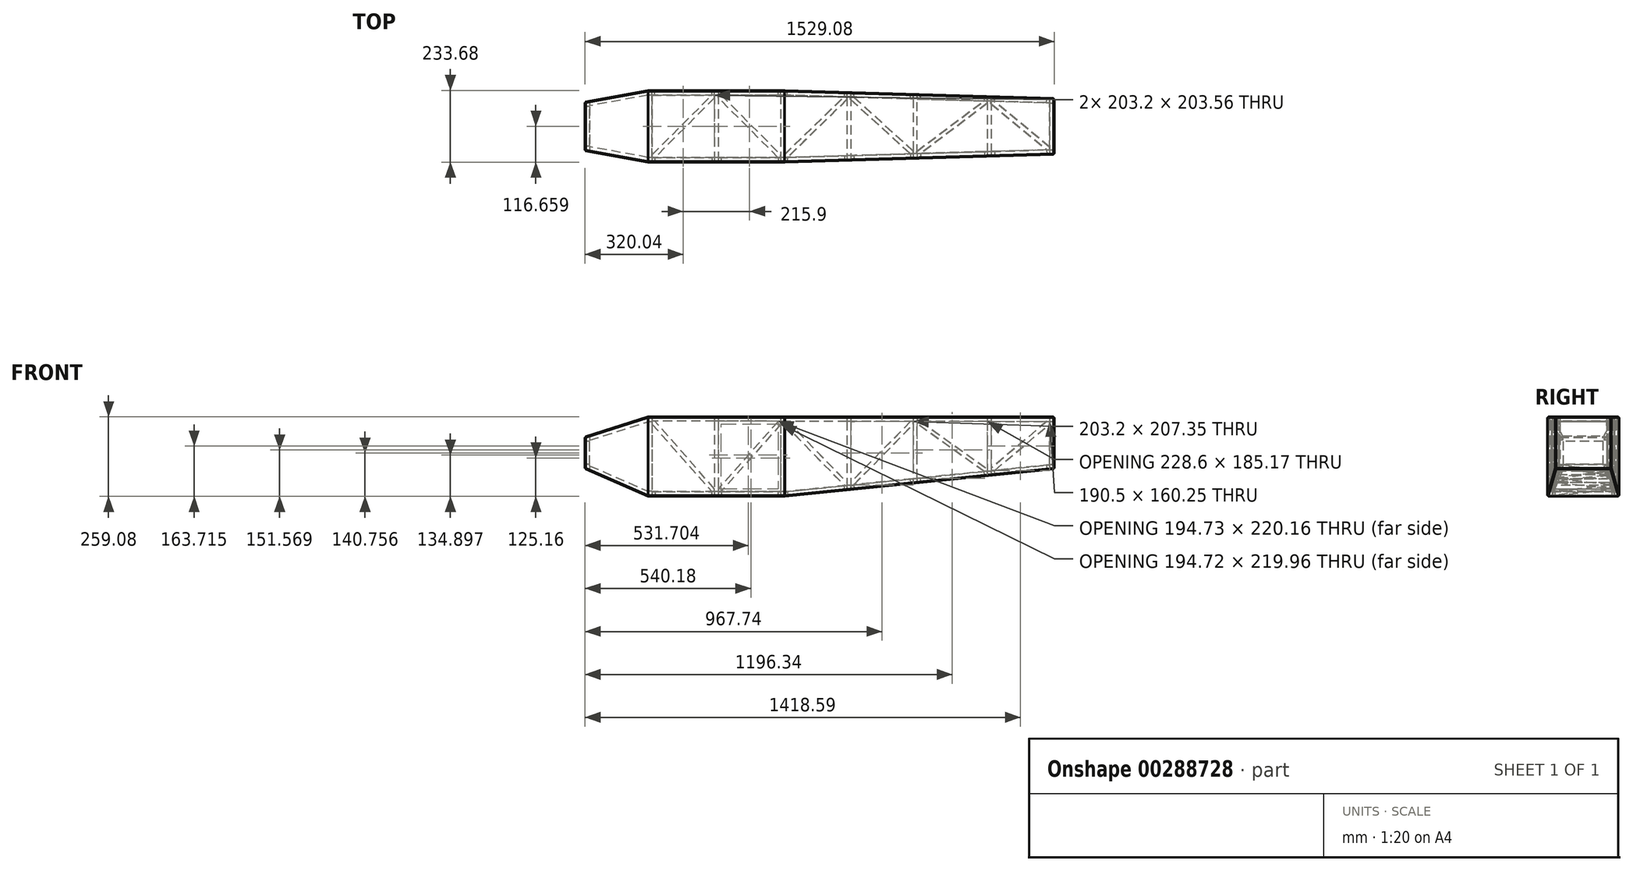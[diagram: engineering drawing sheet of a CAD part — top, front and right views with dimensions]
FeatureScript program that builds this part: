
annotation { "Feature Type Name" : "Feature", "Feature Type Description" : "" }
export const myFeature = defineFeature(function(context is Context, id is Id, definition is map)
    precondition{}
    {
        {
            var Q0;
            Q0=qCreatedBy(makeId("Top.planeOp"),FACE);
            var sketch = newSketch(context, id + "F0", { "sketchPlane" : qUnion([Q0])});
            skLineSegment(sketch, "E0.bottom", {"start": v(762, 177.8) * mm, "end": v(-762, 177.8) * mm});
            skLineSegment(sketch, "E0.top", {"start": v(762, -177.8) * mm, "end": v(-762, -177.8) * mm});
            skLineSegment(sketch, "E0.left", {"start": v(762, 177.8) * mm, "end": v(762, -177.8) * mm});
            skLineSegment(sketch, "E0.right", {"start": v(-762, 177.8) * mm, "end": v(-762, -177.8) * mm});
            skPoint(sketch, "E0.middle", {"position": v(0, 0) * mm});
            skSolve(sketch);
        }
        {
            var Q0;
            Q0=makeQuery(id+"F2.opExtrude","SWEPT_FACE",FACE,{"disambiguationData":[OSD([sQuery(id+"F0.wireOp",EDGE,"E0.top")])]});
            var sketch = newSketch(context, id + "F1", { "sketchPlane" : qUnion([Q0])});
            skLineSegment(sketch, "E1.0", {"start": v(-1003.3, -114.3) * mm, "end": v(1003.3, -114.3) * mm});
            skLineSegment(sketch, "E1.1", {"start": v(-1003.3, 114.3) * mm, "end": v(-1003.3, -114.3) * mm});
            skLineSegment(sketch, "E1.2", {"start": v(1003.3, 114.3) * mm, "end": v(-1003.3, 114.3) * mm});
            skLineSegment(sketch, "E1.3", {"start": v(1003.3, -114.3) * mm, "end": v(1003.3, 114.3) * mm});
            skSolve(sketch);
        }
        {
            var Q0;
            Q0=makeQuery(id+"F0.imprint","IMPRINT",FACE,{"disambiguationData":[TD([[makeQuery(id+"F0.imprint","IMPRINT",EDGE,{"derivedFrom":sQuery(id+"F0.wireOp",EDGE,"E0.bottom")}),1.0]])]});
            extrude(context, id + "F2", {"entities" : qUnion([Q0]), "endBound" : BoundingType.SYMMETRIC, "depth" : 254 * mm});
        }
        {
            var Q0;
            Q0=makeQuery(id+"F2.opExtrude","SWEPT_FACE",FACE,{"disambiguationData":[OSD([sQuery(id+"F0.wireOp",EDGE,"E0.left")])]});
            var sketch = newSketch(context, id + "F3", { "sketchPlane" : qUnion([Q0])});
            skLineSegment(sketch, "E2.0", {"start": v(-165.1, -114.3) * mm, "end": v(165.1, -114.3) * mm});
            skLineSegment(sketch, "E2.1", {"start": v(-165.1, 114.3) * mm, "end": v(-165.1, -114.3) * mm});
            skLineSegment(sketch, "E2.2", {"start": v(165.1, 114.3) * mm, "end": v(-165.1, 114.3) * mm});
            skLineSegment(sketch, "E2.3", {"start": v(165.1, -114.3) * mm, "end": v(165.1, 114.3) * mm});
            skSolve(sketch);
        }
        {
            var Q0;
            Q0=makeQuery(id+"F2.opExtrude","CAP_FACE",FACE,{"disambiguationData":[OSD([sQuery(id+"F0.wireOp",EDGE,"E0.bottom"),sQuery(id+"F0.wireOp",EDGE,"E0.top"),sQuery(id+"F0.wireOp",EDGE,"E0.left"),sQuery(id+"F0.wireOp",EDGE,"E0.right")])],"isStart":false});
            var sketch = newSketch(context, id + "F4", { "sketchPlane" : qUnion([Q0])});
            skLineSegment(sketch, "E3.0", {"start": v(-749.3, -165.1) * mm, "end": v(749.3, -165.1) * mm});
            skLineSegment(sketch, "E3.1", {"start": v(-749.3, 165.1) * mm, "end": v(-749.3, -165.1) * mm});
            skLineSegment(sketch, "E3.2", {"start": v(749.3, 165.1) * mm, "end": v(-749.3, 165.1) * mm});
            skLineSegment(sketch, "E3.3", {"start": v(749.3, -165.1) * mm, "end": v(749.3, 165.1) * mm});
            skSolve(sketch);
        }
        {
            var Q0;
            Q0=qCreatedBy(makeId("Front.planeOp"),FACE);
            var sketch = newSketch(context, id + "F5", { "sketchPlane" : qUnion([Q0])});
            skLineSegment(sketch, "E4.0", {"start": v(-762, 127) * mm, "end": v(-762, -127) * mm, "construction": true});
            skLineSegment(sketch, "E5.bottom", {"start": v(-558.8, -143.07) * mm, "end": v(-546.1, -143.07) * mm});
            skLineSegment(sketch, "E5.top", {"start": v(-558.8, 152.62) * mm, "end": v(-546.1, 152.62) * mm});
            skLineSegment(sketch, "E5.left", {"start": v(-558.8, -143.07) * mm, "end": v(-558.8, 152.62) * mm});
            skLineSegment(sketch, "E5.right", {"start": v(-546.1, -143.07) * mm, "end": v(-546.1, 152.62) * mm});
            skLineSegment(sketch, "E6.bottom", {"start": v(-342.9, -143.07) * mm, "end": v(-330.2, -143.07) * mm});
            skLineSegment(sketch, "E6.top", {"start": v(-342.9, 152.62) * mm, "end": v(-330.2, 152.62) * mm});
            skLineSegment(sketch, "E6.left", {"start": v(-342.9, -143.07) * mm, "end": v(-342.9, 152.62) * mm});
            skLineSegment(sketch, "E6.right", {"start": v(-330.2, -143.07) * mm, "end": v(-330.2, 152.62) * mm});
            skLineSegment(sketch, "E7.bottom", {"start": v(-127, -143.07) * mm, "end": v(-114.3, -143.07) * mm});
            skLineSegment(sketch, "E7.top", {"start": v(-127, 152.62) * mm, "end": v(-114.3, 152.62) * mm});
            skLineSegment(sketch, "E7.left", {"start": v(-127, -143.07) * mm, "end": v(-127, 152.62) * mm});
            skLineSegment(sketch, "E7.right", {"start": v(-114.3, -143.07) * mm, "end": v(-114.3, 152.62) * mm});
            skLineSegment(sketch, "E8.bottom", {"start": v(88.9, -143.07) * mm, "end": v(101.6, -143.07) * mm});
            skLineSegment(sketch, "E8.top", {"start": v(88.9, 152.62) * mm, "end": v(101.6, 152.62) * mm});
            skLineSegment(sketch, "E8.left", {"start": v(88.9, -143.07) * mm, "end": v(88.9, 152.62) * mm});
            skLineSegment(sketch, "E8.right", {"start": v(101.6, -143.07) * mm, "end": v(101.6, 152.62) * mm});
            skLineSegment(sketch, "E9", {"start": v(1356.57, 152.62) * mm, "end": v(-852.45, 152.62) * mm, "construction": true});
            skLineSegment(sketch, "E10", {"start": v(1396.25, -143.07) * mm, "end": v(-846.12, -143.07) * mm, "construction": true});
            skLineSegment(sketch, "E11.bottom", {"start": v(254, 152.62) * mm, "end": v(266.7, 152.62) * mm});
            skLineSegment(sketch, "E11.top", {"start": v(254, -143.07) * mm, "end": v(266.7, -143.07) * mm});
            skLineSegment(sketch, "E12.bottom", {"start": v(546.1, -143.07) * mm, "end": v(558.8, -143.07) * mm});
            skLineSegment(sketch, "E12.top", {"start": v(546.1, 152.62) * mm, "end": v(558.8, 152.62) * mm});
            skLineSegment(sketch, "E12.left", {"start": v(546.1, -143.07) * mm, "end": v(546.1, 152.62) * mm});
            skLineSegment(sketch, "E12.right", {"start": v(558.8, -143.07) * mm, "end": v(558.8, 152.62) * mm});
            skLineSegment(sketch, "E13.bottom", {"start": v(304.8, 152.62) * mm, "end": v(317.5, 152.62) * mm});
            skLineSegment(sketch, "E13.top", {"start": v(304.8, -143.07) * mm, "end": v(317.5, -143.07) * mm});
            skLineSegment(sketch, "E13.left", {"start": v(304.8, 152.62) * mm, "end": v(304.8, -143.07) * mm});
            skLineSegment(sketch, "E13.right", {"start": v(317.5, 152.62) * mm, "end": v(317.5, -143.07) * mm});
            skSolve(sketch);
        }
        {
            var Q0;
            Q0=qSketchRegion(id+"F5",true);
            extrude(context, id + "F6", {"entities" : qUnion([Q0]), "operationType" : NewBodyOperationType.ADD, "endBound" : BoundingType.SYMMETRIC, "depth" : 355.6 * mm});
        }
        {
            var Q0;
            Q0=qCreatedBy(makeId("Front.planeOp"),FACE);
            var sketch = newSketch(context, id + "F7", { "sketchPlane" : qUnion([Q0])});
            skLineSegment(sketch, "E14", {"start": v(-822.55, 43.96) * mm, "end": v(-558.8, 127) * mm});
            skLineSegment(sketch, "E15", {"start": v(-558.8, 127) * mm, "end": v(-1015.01, 307.35) * mm});
            skLineSegment(sketch, "E16", {"start": v(-1015.01, 307.35) * mm, "end": v(-822.55, 43.96) * mm});
            skLineSegment(sketch, "E17.0", {"start": v(-762, 127) * mm, "end": v(-762, -127) * mm, "construction": true});
            skLineSegment(sketch, "E18.0", {"start": v(762, 127) * mm, "end": v(762, -127) * mm, "construction": true});
            skLineSegment(sketch, "E19", {"start": v(-762, -38.1) * mm, "end": v(-558.8, -127) * mm});
            skLineSegment(sketch, "E20", {"start": v(-114.3, -127) * mm, "end": v(762, -38.1) * mm});
            skLineSegment(sketch, "E21", {"start": v(-762, -38.1) * mm, "end": v(-810.44, -38.1) * mm});
            skLineSegment(sketch, "E22", {"start": v(-810.44, -38.1) * mm, "end": v(-810.44, -218.05) * mm});
            skLineSegment(sketch, "E23", {"start": v(-810.44, -218.05) * mm, "end": v(819.71, -218.05) * mm});
            skLineSegment(sketch, "E24", {"start": v(819.71, -218.05) * mm, "end": v(819.71, -38.1) * mm});
            skLineSegment(sketch, "E25", {"start": v(819.71, -38.1) * mm, "end": v(762, -38.1) * mm});
            skLineSegment(sketch, "E26", {"start": v(-114.3, -127) * mm, "end": v(-558.8, -127) * mm});
            skSolve(sketch);
        }
        {
            var Q0;
            Q0=makeQuery(id+"F7.imprint","IMPRINT",FACE,{"disambiguationData":[TD([[makeQuery(id+"F7.imprint","IMPRINT",EDGE,{"derivedFrom":sQuery(id+"F7.wireOp",EDGE,"aae6dbfc-d4bc-4c02-a432-3037b792f5ca")}),1.0]])]});
            var Q1;
            Q1=makeQuery(id+"F7.imprint","IMPRINT",FACE,{"disambiguationData":[TD([[makeQuery(id+"F7.imprint","IMPRINT",EDGE,{"derivedFrom":sQuery(id+"F7.wireOp",EDGE,"E14")}),1.0]])]});
            var Q2;
            Q2=makeQuery(id+"F7.imprint","IMPRINT",FACE,{"disambiguationData":[TD([[makeQuery(id+"F7.imprint","IMPRINT",EDGE,{"derivedFrom":sQuery(id+"F7.wireOp",EDGE,"E19")}),-1.0]])]});
            extrude(context, id + "F8", {"entities" : qUnion([Q0, Q1, Q2]), "operationType" : NewBodyOperationType.REMOVE, "endBound" : BoundingType.SYMMETRIC, "oppositeDirection" : true, "depth" : 381 * mm});
        }
        {
            var Q0;
            Q0=qCreatedBy(makeId("Top.planeOp"),FACE);
            var sketch = newSketch(context, id + "F9", { "sketchPlane" : qUnion([Q0])});
            skLineSegment(sketch, "E27", {"start": v(-925.1, 0) * mm, "end": v(877.17, 0) * mm, "construction": true});
            skLineSegment(sketch, "E28", {"start": v(-885.68, 88.9) * mm, "end": v(840.74, 88.9) * mm, "construction": true});
            skLineSegment(sketch, "E29.0", {"start": v(-762, -177.8) * mm, "end": v(-762, 177.8) * mm, "construction": true});
            skLineSegment(sketch, "E30.0", {"start": v(762, 177.8) * mm, "end": v(762, -177.8) * mm, "construction": true});
            skLineSegment(sketch, "E31.0", {"start": v(-342.9, -368.3) * mm, "end": v(-342.9, -88.9) * mm, "construction": true});
            skLineSegment(sketch, "E32.0", {"start": v(101.6, -177.8) * mm, "end": v(101.6, 177.8) * mm, "construction": true});
            skLineSegment(sketch, "E33", {"start": v(762, 0) * mm, "end": v(762, 88.9) * mm});
            skLineSegment(sketch, "E34.0", {"start": v(-114.3, -177.8) * mm, "end": v(-114.3, 177.8) * mm, "construction": true});
            skLineSegment(sketch, "E35", {"start": v(-762, 77.57) * mm, "end": v(-762, 0) * mm});
            skLineSegment(sketch, "E36", {"start": v(-762, 0) * mm, "end": v(-762, 0) * mm});
            skLineSegment(sketch, "E37.MirrorCS", {"start": v(762, 0) * mm, "end": v(762, -88.9) * mm});
            skLineSegment(sketch, "E38.MirrorCS", {"start": v(-762, -77.57) * mm, "end": v(-762, 0) * mm});
            skLineSegment(sketch, "E39.MirrorCS", {"start": v(-885.68, -88.9) * mm, "end": v(840.74, -88.9) * mm, "construction": true});
            skLineSegment(sketch, "E40.MirrorCS", {"start": v(-762, 177.8) * mm, "end": v(-762, -177.8) * mm, "construction": true});
            skLineSegment(sketch, "E41.MirrorCS", {"start": v(762, -177.8) * mm, "end": v(762, 177.8) * mm, "construction": true});
            skLineSegment(sketch, "E42.MirrorCS", {"start": v(-342.9, 368.3) * mm, "end": v(-342.9, 88.9) * mm, "construction": true});
            skLineSegment(sketch, "E43.MirrorCS", {"start": v(-114.3, 177.8) * mm, "end": v(-114.3, -177.8) * mm, "construction": true});
            skLineSegment(sketch, "E44.MirrorCS", {"start": v(101.6, 177.8) * mm, "end": v(101.6, -177.8) * mm, "construction": true});
            skLineSegment(sketch, "E45.bottom", {"start": v(-858.41, 245.19) * mm, "end": v(858.29, 245.19) * mm});
            skLineSegment(sketch, "E45.top", {"start": v(-858.41, -226.45) * mm, "end": v(858.29, -226.45) * mm});
            skLineSegment(sketch, "E45.left", {"start": v(-858.41, 245.19) * mm, "end": v(-858.41, -226.45) * mm});
            skLineSegment(sketch, "E45.right", {"start": v(858.29, 245.19) * mm, "end": v(858.29, -226.45) * mm});
            skLineSegment(sketch, "E46", {"start": v(-342.9, 114.3) * mm, "end": v(-114.3, 114.3) * mm});
            skLineSegment(sketch, "E47.MirrorCS", {"start": v(-342.9, -114.3) * mm, "end": v(-114.3, -114.3) * mm});
            skLineSegment(sketch, "E48", {"start": v(-342.9, 114.3) * mm, "end": v(-558.8, 114.3) * mm});
            skLineSegment(sketch, "E49", {"start": v(-114.3, 114.3) * mm, "end": v(762, 88.9) * mm});
            skLineSegment(sketch, "E50", {"start": v(-342.9, -114.3) * mm, "end": v(-558.8, -114.3) * mm});
            skLineSegment(sketch, "E51", {"start": v(-114.3, -114.3) * mm, "end": v(762, -88.9) * mm});
            skLineSegment(sketch, "E52", {"start": v(-762, 77.57) * mm, "end": v(-558.8, 114.3) * mm});
            skLineSegment(sketch, "E53", {"start": v(-762, -77.57) * mm, "end": v(-558.8, -114.3) * mm});
            skSolve(sketch);
        }
        {
            var Q0;
            Q0=qSketchRegion(id+"F9",true);
            extrude(context, id + "F10", {"entities" : qUnion([Q0]), "operationType" : NewBodyOperationType.REMOVE, "endBound" : BoundingType.SYMMETRIC, "oppositeDirection" : true, "depth" : 381 * mm});
        }
        {
            var Q0;
            Q0=qCreatedBy(makeId("Top.planeOp"),FACE);
            var sketch = newSketch(context, id + "F11", { "sketchPlane" : qUnion([Q0])});
            skLineSegment(sketch, "E54.1", {"start": v(-749.3, -66.96) * mm, "end": v(-749.3, 66.96) * mm});
            skLineSegment(sketch, "E55.1", {"start": v(749.3, 76.56) * mm, "end": v(749.3, -76.56) * mm});
            skLineSegment(sketch, "E56.0", {"start": v(-127, 101.6) * mm, "end": v(-330.2, 101.6) * mm});
            skLineSegment(sketch, "E57.0", {"start": v(-330.2, -101.96) * mm, "end": v(-127, -101.96) * mm});
            skLineSegment(sketch, "E58.0", {"start": v(558.8, 82.08) * mm, "end": v(749.3, 76.56) * mm});
            skLineSegment(sketch, "E59.0", {"start": v(558.8, -82.08) * mm, "end": v(749.3, -76.56) * mm});
            skLineSegment(sketch, "E60.0", {"start": v(-749.3, -66.96) * mm, "end": v(-558.8, -101.4) * mm});
            skLineSegment(sketch, "E61", {"start": v(-342.9, -101.96) * mm, "end": v(-546.1, -101.96) * mm});
            skLineSegment(sketch, "E62", {"start": v(-546.1, 101.6) * mm, "end": v(-342.9, 101.6) * mm});
            skLineSegment(sketch, "E63.0.1", {"start": v(-546.1, -101.96) * mm, "end": v(-546.1, 101.6) * mm});
            skLineSegment(sketch, "E63.0.3", {"start": v(-558.8, 101.4) * mm, "end": v(-558.8, -101.4) * mm});
            skLineSegment(sketch, "E64.0.1", {"start": v(-342.9, 101.6) * mm, "end": v(-342.9, -101.96) * mm});
            skLineSegment(sketch, "E65.0.1", {"start": v(88.9, 95.71) * mm, "end": v(88.9, -95.7) * mm});
            skLineSegment(sketch, "E65.0.3", {"start": v(101.6, -95.34) * mm, "end": v(101.6, 95.34) * mm});
            skLineSegment(sketch, "E66.0.1", {"start": v(304.8, 89.45) * mm, "end": v(304.8, -89.45) * mm});
            skLineSegment(sketch, "E66.0.3", {"start": v(317.5, -89.08) * mm, "end": v(317.5, 89.08) * mm});
            skLineSegment(sketch, "E67.0.1", {"start": v(546.1, 82.45) * mm, "end": v(546.1, -82.45) * mm});
            skLineSegment(sketch, "E67.0.3", {"start": v(558.8, -82.08) * mm, "end": v(558.8, 82.08) * mm});
            skLineSegment(sketch, "E68.trimOffspring", {"start": v(304.8, -89.45) * mm, "end": v(101.6, -95.34) * mm});
            skLineSegment(sketch, "E69.trimOffspring", {"start": v(88.9, -95.7) * mm, "end": v(-114.3, -101.6) * mm});
            skLineSegment(sketch, "E70.trimOffspring", {"start": v(101.6, 95.34) * mm, "end": v(304.8, 89.45) * mm});
            skPoint(sketch, "E63.0.2.end.orphan", {"position": v(-558.8, 114.3) * mm});
            skPoint(sketch, "E63.0.2.start.orphan", {"position": v(-546.1, 114.3) * mm});
            skPoint(sketch, "E71.orphan", {"position": v(-558.8, -114.3) * mm});
            skPoint(sketch, "E72.orphan", {"position": v(-546.1, -114.3) * mm});
            skLineSegment(sketch, "E73", {"start": v(-749.3, 66.96) * mm, "end": v(-558.8, 101.4) * mm});
            skLineSegment(sketch, "E74", {"start": v(-114.3, -101.6) * mm, "end": v(-114.3, 101.6) * mm});
            skLineSegment(sketch, "E75", {"start": v(-330.2, 101.6) * mm, "end": v(-330.2, -101.96) * mm});
            skLineSegment(sketch, "E76", {"start": v(-127, 101.6) * mm, "end": v(-127, -101.96) * mm});
            skLineSegment(sketch, "E77", {"start": v(546.1, -82.45) * mm, "end": v(317.5, -89.08) * mm});
            skLineSegment(sketch, "E78", {"start": v(88.9, 95.71) * mm, "end": v(-114.3, 101.6) * mm});
            skLineSegment(sketch, "E79", {"start": v(546.1, 82.45) * mm, "end": v(317.5, 89.08) * mm});
            skSolve(sketch);
        }
        {
            var Q0;
            Q0=qSketchRegion(id+"F11",true);
            extrude(context, id + "F12", {"entities" : qUnion([Q0]), "operationType" : NewBodyOperationType.REMOVE, "endBound" : BoundingType.SYMMETRIC, "depth" : 381 * mm});
        }
        {
            var Q0;
            Q0=qCreatedBy(makeId("Front.planeOp"),FACE);
            var sketch = newSketch(context, id + "F13", { "sketchPlane" : qUnion([Q0])});
            skLineSegment(sketch, "E80.0", {"start": v(-749.3, 53.7) * mm, "end": v(-558.8, 113.69) * mm});
            skLineSegment(sketch, "E80.1", {"start": v(-749.3, -29.8) * mm, "end": v(-749.3, 53.7) * mm});
            skLineSegment(sketch, "E80.2", {"start": v(-749.3, -29.8) * mm, "end": v(-558.8, -113.14) * mm});
            skLineSegment(sketch, "E80.3", {"start": v(-342.9, -114.3) * mm, "end": v(-546.1, -114.3) * mm});
            skLineSegment(sketch, "E81.0", {"start": v(749.3, -26.62) * mm, "end": v(558.8, -45.95) * mm});
            skLineSegment(sketch, "E81.1", {"start": v(749.3, -26.62) * mm, "end": v(749.3, 114.3) * mm});
            skLineSegment(sketch, "E81.2", {"start": v(558.8, 114.3) * mm, "end": v(749.3, 114.3) * mm});
            skLineSegment(sketch, "E82", {"start": v(-127, -114.36) * mm, "end": v(-330.2, -114.3) * mm});
            skLineSegment(sketch, "E83.0.1", {"start": v(558.8, 114.3) * mm, "end": v(558.8, -45.95) * mm});
            skLineSegment(sketch, "E84.0.1", {"start": v(101.6, 114.89) * mm, "end": v(101.6, -92.46) * mm});
            skLineSegment(sketch, "E84.0.3", {"start": v(304.8, -71.84) * mm, "end": v(304.8, 114.63) * mm});
            skLineSegment(sketch, "E85.0.0", {"start": v(-330.2, 115.44) * mm, "end": v(-330.2, -114.3) * mm});
            skLineSegment(sketch, "E85.0.2", {"start": v(-127, -114.36) * mm, "end": v(-127, 115.18) * mm});
            skLineSegment(sketch, "E86.0.1", {"start": v(-546.1, 115.71) * mm, "end": v(-546.1, -114.3) * mm});
            skLineSegment(sketch, "E86.0.3", {"start": v(-342.9, -114.3) * mm, "end": v(-342.9, 115.45) * mm});
            skLineSegment(sketch, "E87.0.2", {"start": v(-558.8, -113.14) * mm, "end": v(-558.8, 113.69) * mm});
            skPoint(sketch, "E83.0.0.start.orphan", {"position": v(749.3, 127) * mm});
            skPoint(sketch, "E88.orphan", {"position": v(558.8, 127) * mm});
            skPoint(sketch, "E89.0.0.start.orphan", {"position": v(558.8, 126.99) * mm});
            skLineSegment(sketch, "E90.trimOffspring", {"start": v(304.8, 114.63) * mm, "end": v(101.6, 114.89) * mm});
            skPoint(sketch, "E84.0.0.start.orphan", {"position": v(304.8, 127) * mm});
            skLineSegment(sketch, "E91.trimOffspring", {"start": v(-127, 115.18) * mm, "end": v(-330.2, 115.44) * mm});
            skPoint(sketch, "E85.0.1.end.orphan", {"position": v(-127, -127) * mm});
            skPoint(sketch, "E92.orphan", {"position": v(-330.2, -127) * mm});
            skLineSegment(sketch, "E93.trimOffspring", {"start": v(-342.9, 115.45) * mm, "end": v(-546.1, 115.71) * mm});
            skPoint(sketch, "E85.0.3.end.orphan", {"position": v(-330.2, 127) * mm});
            skPoint(sketch, "E85.0.3.start.orphan", {"position": v(-127, 127) * mm});
            skPoint(sketch, "E86.0.2.end.orphan", {"position": v(-342.9, -127) * mm});
            skPoint(sketch, "E94.orphan", {"position": v(-546.1, -127) * mm});
            skPoint(sketch, "E95.orphan", {"position": v(-546.1, 127) * mm});
            skPoint(sketch, "E87.0.3.start.orphan", {"position": v(-558.8, 127) * mm});
            skPoint(sketch, "E96.orphan", {"position": v(101.6, 127) * mm});
            skLineSegment(sketch, "E97", {"start": v(546.1, -48.1) * mm, "end": v(456.3, -56.47) * mm});
            skPoint(sketch, "E83.0.2.end.orphan", {"position": v(749.3, -39.39) * mm});
            skPoint(sketch, "E98.orphan", {"position": v(-342.9, 127) * mm});
            skLineSegment(sketch, "E99.left", {"start": v(-680.76, 244.02) * mm, "end": v(-680.76, 242.67) * mm});
            skLineSegment(sketch, "E99.right", {"start": v(-640.08, 244.02) * mm, "end": v(-640.08, 242.67) * mm});
            skLineSegment(sketch, "E100.bottom", {"start": v(851.63, 270.75) * mm, "end": v(-718.73, 270.75) * mm});
            skLineSegment(sketch, "E100.top", {"start": v(851.63, 127) * mm, "end": v(-718.73, 127) * mm});
            skLineSegment(sketch, "E100.left", {"start": v(851.63, 270.75) * mm, "end": v(851.63, 127) * mm});
            skLineSegment(sketch, "E100.right", {"start": v(-718.73, 270.75) * mm, "end": v(-718.73, 127) * mm});
            skLineSegment(sketch, "E101", {"start": v(-114.3, -114.36) * mm, "end": v(88.9, -93.75) * mm});
            skLineSegment(sketch, "E102", {"start": v(546.1, 114.3) * mm, "end": v(317.5, 114.61) * mm});
            skLineSegment(sketch, "E103", {"start": v(88.9, 114.9) * mm, "end": v(-114.3, 115.18) * mm});
            skLineSegment(sketch, "E104", {"start": v(-114.3, 115.18) * mm, "end": v(-114.3, -114.36) * mm});
            skLineSegment(sketch, "E105", {"start": v(88.9, 114.9) * mm, "end": v(88.9, -93.75) * mm});
            skLineSegment(sketch, "E106", {"start": v(317.5, 114.61) * mm, "end": v(317.5, -70.55) * mm});
            skLineSegment(sketch, "E107", {"start": v(546.1, 114.3) * mm, "end": v(546.1, -48.1) * mm});
            skLineSegment(sketch, "E108.trimOffspring", {"start": v(317.5, -70.55) * mm, "end": v(456.3, -56.47) * mm});
            skLineSegment(sketch, "E109.trimOffspring", {"start": v(101.6, -92.46) * mm, "end": v(304.8, -71.84) * mm});
            skSolve(sketch);
        }
        {
            var Q0;
            Q0=qSketchRegion(id+"F13",true);
            extrude(context, id + "F14", {"entities" : qUnion([Q0]), "operationType" : NewBodyOperationType.REMOVE, "endBound" : BoundingType.SYMMETRIC, "oppositeDirection" : true, "depth" : 381 * mm});
        }
        {
            var Q0;
            {var subQ4=sQuery(id+"F5.wireOp",EDGE,"E5.top");var subQ11=sQuery(id+"F5.wireOp",EDGE,"E5.left");Q0=makeQuery(id+"F14.boolean.opBoolean","MERGE",FACE,{"derivedFrom":[makeQuery(id+"F12.boolean.opBoolean","MERGE",FACE,{"derivedFrom":[makeQuery(id+"F6.boolean.opBoolean","SPLIT",FACE,{"disambiguationData":[TD([makeQuery(id+"F6.opExtrude","SWEPT_FACE",FACE,{"disambiguationData":[OSD([subQ4])]})])],"derivedFrom":makeQuery(id+"F6.opExtrude","SWEPT_FACE",FACE,{"disambiguationData":[OSD([subQ11])]})}),makeQuery(id+"F12.opExtrude","SWEPT_FACE",FACE,{"disambiguationData":[OSD([sQuery(id+"F11.wireOp",EDGE,"76c89935-962c-43c5-8293-adbbc792d1c5.0")])]})]}),makeQuery(id+"F14.opExtrude","SWEPT_FACE",FACE,{"disambiguationData":[OSD([sQuery(id+"F13.wireOp",EDGE,"9ef2c277-a94d-4be6-9fd4-f6ea86bf56da.0.3")])]})]});}
            var sketch = newSketch(context, id + "F15", { "sketchPlane" : qUnion([Q0])});
            skLineSegment(sketch, "E110.bottom", {"start": v(-101.4, 113.69) * mm, "end": v(101.4, 113.69) * mm});
            skLineSegment(sketch, "E110.top", {"start": v(-101.4, -113.14) * mm, "end": v(101.4, -113.14) * mm});
            skLineSegment(sketch, "E110.left", {"start": v(-101.4, 113.69) * mm, "end": v(-101.4, -113.14) * mm});
            skLineSegment(sketch, "E110.right", {"start": v(101.4, 113.69) * mm, "end": v(101.4, -113.14) * mm});
            skSolve(sketch);
        }
        {
            var Q0;
            Q0=qSketchRegion(id+"F15",true);
            extrude(context, id + "F16", {"entities" : qUnion([Q0]), "operationType" : NewBodyOperationType.REMOVE, "oppositeDirection" : true, "depth" : 25.4 * mm});
        }
        {
            var Q0;
            {var subQ1=sQuery(id+"F5.wireOp",EDGE,"E6.left");var subQ2=sQuery(id+"F5.wireOp",EDGE,"E6.top");Q0=makeQuery(id+"F14.boolean.opBoolean","MERGE",FACE,{"derivedFrom":[makeQuery(id+"F12.boolean.opBoolean","MERGE",FACE,{"derivedFrom":[makeQuery(id+"F6.boolean.opBoolean","SPLIT",FACE,{"disambiguationData":[TD([makeQuery(id+"F6.opExtrude","SWEPT_FACE",FACE,{"disambiguationData":[OSD([subQ2])]})])],"derivedFrom":makeQuery(id+"F6.opExtrude","SWEPT_FACE",FACE,{"disambiguationData":[OSD([subQ1])]})}),makeQuery(id+"F12.opExtrude","SWEPT_FACE",FACE,{"disambiguationData":[OSD([sQuery(id+"F11.wireOp",EDGE,"7b3102ac-ed15-4f5d-bc17-57cfcd7eebf1.0")])]})]}),makeQuery(id+"F14.opExtrude","SWEPT_FACE",FACE,{"disambiguationData":[OSD([sQuery(id+"F13.wireOp",EDGE,"8vpACN4d-Oada-hr1t-Xb63-NezVnV2j5PEM")])]})]});}
            var sketch = newSketch(context, id + "F17", { "sketchPlane" : qUnion([Q0])});
            skLineSegment(sketch, "E111.bottom", {"start": v(-101.6, 115.45) * mm, "end": v(101.96, 115.45) * mm});
            skLineSegment(sketch, "E111.top", {"start": v(-101.6, -114.3) * mm, "end": v(101.96, -114.3) * mm});
            skLineSegment(sketch, "E111.left", {"start": v(-101.6, 115.45) * mm, "end": v(-101.6, -114.3) * mm});
            skLineSegment(sketch, "E111.right", {"start": v(101.96, 115.45) * mm, "end": v(101.96, -114.3) * mm});
            skSolve(sketch);
        }
        {
            var Q0;
            Q0=qSketchRegion(id+"F17",true);
            extrude(context, id + "F18", {"entities" : qUnion([Q0]), "operationType" : NewBodyOperationType.REMOVE, "oppositeDirection" : true, "depth" : 25.4 * mm});
        }
        {
            var Q0;
            {var subQ8=sQuery(id+"F5.wireOp",EDGE,"E7.top");var subQ16=sQuery(id+"F5.wireOp",EDGE,"E7.left");Q0=makeQuery(id+"F14.boolean.opBoolean","MERGE",FACE,{"derivedFrom":[makeQuery(id+"F12.boolean.opBoolean","MERGE",FACE,{"derivedFrom":[makeQuery(id+"F6.boolean.opBoolean","SPLIT",FACE,{"disambiguationData":[TD([makeQuery(id+"F6.opExtrude","SWEPT_FACE",FACE,{"disambiguationData":[OSD([subQ8])]})])],"derivedFrom":makeQuery(id+"F6.opExtrude","SWEPT_FACE",FACE,{"disambiguationData":[OSD([subQ16])]})}),makeQuery(id+"F12.opExtrude","SWEPT_FACE",FACE,{"disambiguationData":[OSD([sQuery(id+"F11.wireOp",EDGE,"b35c1112-db7b-4928-a18e-9a17467dcdab.0")])]})]}),makeQuery(id+"F14.opExtrude","SWEPT_FACE",FACE,{"disambiguationData":[OSD([sQuery(id+"F13.wireOp",EDGE,"fa40cc79-636a-4cbc-a25d-f27d8fe22ac2.0.3")])]})]});}
            var sketch = newSketch(context, id + "F19", { "sketchPlane" : qUnion([Q0])});
            skLineSegment(sketch, "E112.bottom", {"start": v(-101.6, 115.18) * mm, "end": v(101.96, 115.18) * mm});
            skLineSegment(sketch, "E112.top", {"start": v(-101.6, -114.36) * mm, "end": v(101.96, -114.36) * mm});
            skLineSegment(sketch, "E112.left", {"start": v(-101.6, 115.18) * mm, "end": v(-101.6, -114.36) * mm});
            skLineSegment(sketch, "E112.right", {"start": v(101.96, 115.18) * mm, "end": v(101.96, -114.36) * mm});
            skSolve(sketch);
        }
        {
            var Q0;
            Q0=qSketchRegion(id+"F19",true);
            extrude(context, id + "F20", {"entities" : qUnion([Q0]), "operationType" : NewBodyOperationType.REMOVE, "oppositeDirection" : true, "depth" : 25.4 * mm});
        }
        {
            var Q0;
            {var subQ0=sQuery(id+"F5.wireOp",EDGE,"E8.bottom");var subQ36=sQuery(id+"F5.wireOp",EDGE,"E8.left");var subQ37=sQuery(id+"F5.wireOp",EDGE,"E8.top");var subQ60=makeQuery(id+"F6.opExtrude","SWEPT_FACE",FACE,{"disambiguationData":[OSD([subQ36])]});Q0=makeQuery(id+"F14.boolean.opBoolean","MERGE",FACE,{"derivedFrom":[makeQuery(id+"F12.boolean.opBoolean","MERGE",FACE,{"derivedFrom":[makeQuery(id+"F6.boolean.opBoolean","SPLIT",FACE,{"disambiguationData":[TD([makeQuery(id+"F6.opExtrude","SWEPT_FACE",FACE,{"disambiguationData":[OSD([subQ37])]})])],"derivedFrom":subQ60}),makeQuery(id+"F6.boolean.opBoolean","SPLIT",FACE,{"disambiguationData":[TD([makeQuery(id+"F6.opExtrude","SWEPT_FACE",FACE,{"disambiguationData":[OSD([subQ0])]})])],"derivedFrom":subQ60}),makeQuery(id+"F12.opExtrude","SWEPT_FACE",FACE,{"disambiguationData":[OSD([sQuery(id+"F11.wireOp",EDGE,"7310f20e-b108-4276-8773-8cf4f74fe12c.0")])]})]}),makeQuery(id+"F14.opExtrude","SWEPT_FACE",FACE,{"disambiguationData":[OSD([sQuery(id+"F13.wireOp",EDGE,"FrRoJ9V7-tiAn-pTb4-UzEj-WxOpO9FH2ecp")])]})]});}
            var sketch = newSketch(context, id + "F21", { "sketchPlane" : qUnion([Q0])});
            skLineSegment(sketch, "E113.bottom", {"start": v(-95.71, 114.9) * mm, "end": v(95.7, 114.9) * mm});
            skLineSegment(sketch, "E113.top", {"start": v(-95.71, -93.75) * mm, "end": v(95.7, -93.75) * mm});
            skLineSegment(sketch, "E113.left", {"start": v(-95.71, 114.9) * mm, "end": v(-95.71, -93.75) * mm});
            skLineSegment(sketch, "E113.right", {"start": v(95.7, 114.9) * mm, "end": v(95.7, -93.75) * mm});
            skSolve(sketch);
        }
        {
            var Q0;
            Q0=qSketchRegion(id+"F21",true);
            extrude(context, id + "F22", {"entities" : qUnion([Q0]), "operationType" : NewBodyOperationType.REMOVE, "oppositeDirection" : true, "depth" : 25.4 * mm});
        }
        {
            var Q0;
            {var subQ35=sQuery(id+"F5.wireOp",EDGE,"E13.left");var subQ37=sQuery(id+"F5.wireOp",EDGE,"E13.bottom");Q0=makeQuery(id+"F14.boolean.opBoolean","MERGE",FACE,{"derivedFrom":[makeQuery(id+"F12.boolean.opBoolean","MERGE",FACE,{"derivedFrom":[makeQuery(id+"F6.boolean.opBoolean","SPLIT",FACE,{"disambiguationData":[TD([makeQuery(id+"F6.opExtrude","SWEPT_FACE",FACE,{"disambiguationData":[OSD([subQ37])]})])],"derivedFrom":makeQuery(id+"F6.opExtrude","SWEPT_FACE",FACE,{"disambiguationData":[OSD([subQ35])]})}),makeQuery(id+"F12.opExtrude","SWEPT_FACE",FACE,{"disambiguationData":[OSD([sQuery(id+"F11.wireOp",EDGE,"b7ba8543-acbf-43cf-88d8-2159336d2e7e.0")])]})]}),makeQuery(id+"F14.opExtrude","SWEPT_FACE",FACE,{"disambiguationData":[OSD([sQuery(id+"F13.wireOp",EDGE,"MzW9eNza-KUkf-pAGu-OPrh-YCygVrhiN9A4")])]})]});}
            var sketch = newSketch(context, id + "F23", { "sketchPlane" : qUnion([Q0])});
            skLineSegment(sketch, "E114.bottom", {"start": v(-89.45, 114.63) * mm, "end": v(89.45, 114.63) * mm});
            skLineSegment(sketch, "E114.top", {"start": v(-89.45, -71.84) * mm, "end": v(89.45, -71.84) * mm});
            skLineSegment(sketch, "E114.left", {"start": v(-89.45, 114.63) * mm, "end": v(-89.45, -71.84) * mm});
            skLineSegment(sketch, "E114.right", {"start": v(89.45, 114.63) * mm, "end": v(89.45, -71.84) * mm});
            skSolve(sketch);
        }
        {
            var Q0;
            Q0=qSketchRegion(id+"F23",true);
            extrude(context, id + "F24", {"entities" : qUnion([Q0]), "operationType" : NewBodyOperationType.REMOVE, "oppositeDirection" : true, "depth" : 15.24 * mm});
        }
        {
            var Q0;
            {var subQ18=sQuery(id+"F5.wireOp",EDGE,"E12.left");var subQ19=sQuery(id+"F5.wireOp",EDGE,"E12.top");Q0=makeQuery(id+"F14.boolean.opBoolean","MERGE",FACE,{"derivedFrom":[makeQuery(id+"F12.boolean.opBoolean","MERGE",FACE,{"derivedFrom":[makeQuery(id+"F6.boolean.opBoolean","SPLIT",FACE,{"disambiguationData":[TD([makeQuery(id+"F6.opExtrude","SWEPT_FACE",FACE,{"disambiguationData":[OSD([subQ19])]})])],"derivedFrom":makeQuery(id+"F6.opExtrude","SWEPT_FACE",FACE,{"disambiguationData":[OSD([subQ18])]})}),makeQuery(id+"F12.opExtrude","SWEPT_FACE",FACE,{"disambiguationData":[OSD([sQuery(id+"F11.wireOp",EDGE,"94f42aec-5a63-4bb3-a17e-c23af455982a.0")])]})]}),makeQuery(id+"F14.opExtrude","SWEPT_FACE",FACE,{"disambiguationData":[OSD([sQuery(id+"F13.wireOp",EDGE,"4bo9Z2lR-88Dg-C45D-lGNA-9ZzvTnCFj7b6")])]})]});}
            var sketch = newSketch(context, id + "F25", { "sketchPlane" : qUnion([Q0])});
            skLineSegment(sketch, "E115.bottom", {"start": v(-82.45, 114.3) * mm, "end": v(82.45, 114.3) * mm});
            skLineSegment(sketch, "E115.top", {"start": v(-82.45, -48.1) * mm, "end": v(82.45, -48.1) * mm});
            skLineSegment(sketch, "E115.left", {"start": v(82.45, 114.3) * mm, "end": v(82.45, -48.1) * mm});
            skLineSegment(sketch, "E115.right", {"start": v(-82.45, 114.3) * mm, "end": v(-82.45, -48.1) * mm});
            skSolve(sketch);
        }
        {
            var Q0;
            Q0=qSketchRegion(id+"F25",true);
            extrude(context, id + "F26", {"entities" : qUnion([Q0]), "operationType" : NewBodyOperationType.REMOVE, "oppositeDirection" : true, "depth" : 13.97 * mm});
        }
        {
            var Q0;
            Q0=makeQuery(id+"F14.boolean.opBoolean","MERGE",FACE,{"derivedFrom":[makeQuery(id+"F12.boolean.opBoolean","COPY",FACE,{"derivedFrom":makeQuery(id+"F12.opExtrude","SWEPT_FACE",FACE,{"disambiguationData":[OSD([sQuery(id+"F11.wireOp",EDGE,"adecc727-4d20-49de-aa06-e82a0813468d.1")])]})}),makeQuery(id+"F14.opExtrude","SWEPT_FACE",FACE,{"disambiguationData":[OSD([sQuery(id+"F13.wireOp",EDGE,"9f7ba322-1395-4fc7-9540-b671459040af.2")])]})]});
            var sketch = newSketch(context, id + "F27", { "sketchPlane" : qUnion([Q0])});
            skLineSegment(sketch, "E116.bottom", {"start": v(-114.91, 114.3) * mm, "end": v(114.6, 114.3) * mm});
            skLineSegment(sketch, "E116.top", {"start": v(-114.91, -7.58) * mm, "end": v(114.6, -7.58) * mm});
            skLineSegment(sketch, "E116.left", {"start": v(-114.91, 114.3) * mm, "end": v(-114.91, -7.58) * mm});
            skLineSegment(sketch, "E116.right", {"start": v(114.6, 114.3) * mm, "end": v(114.6, -7.58) * mm});
            skSolve(sketch);
        }
        {
            var Q0;
            Q0=makeQuery(id+"F2.opExtrude","SWEPT_FACE",FACE,{"disambiguationData":[OSD([sQuery(id+"F0.wireOp",EDGE,"E0.right")])]});
            var sketch = newSketch(context, id + "F28", { "sketchPlane" : qUnion([Q0])});
            skLineSegment(sketch, "E117.0", {"start": v(-64.87, 50.32) * mm, "end": v(64.87, 50.32) * mm});
            skLineSegment(sketch, "E118.0", {"start": v(-64.87, -25.4) * mm, "end": v(-64.87, 50.32) * mm});
            skLineSegment(sketch, "E118.1", {"start": v(-64.87, -25.4) * mm, "end": v(64.87, -25.4) * mm});
            skLineSegment(sketch, "E118.2", {"start": v(64.87, -25.4) * mm, "end": v(64.87, 50.32) * mm});
            skSolve(sketch);
        }
        {
            var Q0;
            Q0=qSketchRegion(id+"F28",true);
            extrude(context, id + "F29", {"entities" : qUnion([Q0]), "operationType" : NewBodyOperationType.REMOVE, "oppositeDirection" : true, "depth" : 25.4 * mm});
        }
        {
            var Q0;
            Q0=makeQuery(id+"F2.opExtrude","SWEPT_FACE",FACE,{"disambiguationData":[OSD([sQuery(id+"F0.wireOp",EDGE,"E0.left")])]});
            var sketch = newSketch(context, id + "F30", { "sketchPlane" : qUnion([Q0])});
            skLineSegment(sketch, "E119.bottom", {"start": v(-76.2, 114.3) * mm, "end": v(76.2, 114.3) * mm});
            skLineSegment(sketch, "E119.top", {"start": v(-76.2, -25.4) * mm, "end": v(76.2, -25.4) * mm});
            skLineSegment(sketch, "E119.left", {"start": v(-76.2, 114.3) * mm, "end": v(-76.2, -25.4) * mm});
            skLineSegment(sketch, "E119.right", {"start": v(76.2, 114.3) * mm, "end": v(76.2, -25.4) * mm});
            skSolve(sketch);
        }
        {
            var Q0;
            Q0=makeQuery(id+"F30.imprint","IMPRINT",FACE,{"disambiguationData":[TD([[makeQuery(id+"F30.imprint","IMPRINT",EDGE,{"derivedFrom":sQuery(id+"F30.wireOp",EDGE,"E119.bottom")}),-1.0]])]});
            extrude(context, id + "F31", {"entities" : qUnion([Q0]), "operationType" : NewBodyOperationType.REMOVE, "oppositeDirection" : true, "depth" : 12.7 * mm});
        }
        {
            var Q0;
            Q0=makeQuery(id+"F10.boolean.opBoolean","COPY",FACE,{"derivedFrom":makeQuery(id+"F10.opExtrude","SWEPT_FACE",FACE,{"disambiguationData":[OSD([sQuery(id+"F9.wireOp",EDGE,"E51")])]})});
            var sketch = newSketch(context, id + "F32", { "sketchPlane" : qUnion([Q0])});
            skLineSegment(sketch, "E120", {"start": v(746.4, 114.3) * mm, "end": v(555.82, -45.95) * mm, "construction": true});
            skLineSegment(sketch, "E121", {"start": v(543.11, -48.1) * mm, "end": v(314.42, 114.61) * mm, "construction": true});
            skLineSegment(sketch, "E122", {"start": v(301.71, 114.63) * mm, "end": v(98.43, -92.46) * mm, "construction": true});
            skLineSegment(sketch, "E123", {"start": v(85.72, -93.75) * mm, "end": v(-117.56, 115.18) * mm, "construction": true});
            skLineSegment(sketch, "E124", {"start": v(746.4, 106) * mm, "end": v(567.04, -44.81) * mm});
            skLineSegment(sketch, "E125", {"start": v(533.43, -49) * mm, "end": v(314.42, 106.82) * mm});
            skLineSegment(sketch, "E126", {"start": v(108.3, -91.45) * mm, "end": v(301.71, 105.56) * mm});
            skLineSegment(sketch, "E127", {"start": v(-117.56, 106.07) * mm, "end": v(77.66, -94.56) * mm});
            skLineSegment(sketch, "E128.MirrorCS", {"start": v(736.53, 114.3) * mm, "end": v(558.87, -35.1) * mm});
            skLineSegment(sketch, "E129.MirrorCS", {"start": v(540.8, -38.66) * mm, "end": v(325.4, 114.6) * mm});
            skLineSegment(sketch, "E130.MirrorCS", {"start": v(99.25, -82.56) * mm, "end": v(292.65, 114.46) * mm});
            skLineSegment(sketch, "E131.MirrorCS", {"start": v(-108.46, 114.93) * mm, "end": v(85.72, -84.64) * mm});
            skPoint(sketch, "E132", {"position": v(736.53, 114.3) * mm});
            skPoint(sketch, "E133", {"position": v(325.4, 114.6) * mm});
            skPoint(sketch, "E134", {"position": v(85.72, -84.64) * mm});
            skPoint(sketch, "E135.orphan", {"position": v(738.23, 115.72) * mm});
            skLineSegment(sketch, "E136", {"start": v(558.87, -35.1) * mm, "end": v(555.82, -37.65) * mm});
            skLineSegment(sketch, "E137", {"start": v(540.8, -38.66) * mm, "end": v(543.11, -40.3) * mm});
            skPoint(sketch, "E138.orphan", {"position": v(321.78, 117.17) * mm});
            skLineSegment(sketch, "E139", {"start": v(292.65, 114.46) * mm, "end": v(292.83, 114.64) * mm});
            skLineSegment(sketch, "E140", {"start": v(99.25, -82.56) * mm, "end": v(98.43, -83.4) * mm});
            skPoint(sketch, "E141.orphan", {"position": v(86.76, -85.7) * mm});
            skLineSegment(sketch, "E142", {"start": v(-108.46, 114.93) * mm, "end": v(-108.7, 115.17) * mm});
            skLineSegment(sketch, "E143", {"start": v(-108.7, 115.17) * mm, "end": v(-117.56, 115.18) * mm});
            skLineSegment(sketch, "E144", {"start": v(-117.56, 115.18) * mm, "end": v(-117.56, 106.07) * mm});
            skLineSegment(sketch, "E145", {"start": v(85.72, -84.64) * mm, "end": v(85.72, -93.75) * mm});
            skLineSegment(sketch, "E146", {"start": v(77.66, -94.56) * mm, "end": v(85.72, -93.75) * mm});
            skLineSegment(sketch, "E147", {"start": v(98.43, -83.4) * mm, "end": v(98.43, -92.46) * mm});
            skLineSegment(sketch, "E148", {"start": v(108.3, -91.45) * mm, "end": v(98.43, -92.46) * mm});
            skLineSegment(sketch, "E149", {"start": v(301.71, 105.56) * mm, "end": v(301.71, 114.63) * mm});
            skLineSegment(sketch, "E150", {"start": v(292.83, 114.64) * mm, "end": v(301.71, 114.63) * mm});
            skLineSegment(sketch, "E151", {"start": v(325.4, 114.6) * mm, "end": v(314.42, 114.61) * mm});
            skLineSegment(sketch, "E152", {"start": v(314.42, 106.82) * mm, "end": v(314.42, 114.61) * mm});
            skLineSegment(sketch, "E153", {"start": v(533.43, -49) * mm, "end": v(543.11, -48.1) * mm});
            skLineSegment(sketch, "E154", {"start": v(543.11, -40.3) * mm, "end": v(543.11, -48.1) * mm});
            skLineSegment(sketch, "E155", {"start": v(555.82, -37.65) * mm, "end": v(555.82, -45.95) * mm});
            skLineSegment(sketch, "E156", {"start": v(567.04, -44.81) * mm, "end": v(555.82, -45.95) * mm});
            skLineSegment(sketch, "E157", {"start": v(746.4, 106) * mm, "end": v(746.4, 114.3) * mm});
            skLineSegment(sketch, "E158", {"start": v(736.53, 114.3) * mm, "end": v(746.4, 114.3) * mm});
            skSolve(sketch);
        }
        {
            var Q0;
            Q0=makeQuery(id+"F10.boolean.opBoolean","COPY",FACE,{"derivedFrom":makeQuery(id+"F10.opExtrude","SWEPT_FACE",FACE,{"disambiguationData":[OSD([sQuery(id+"F9.wireOp",EDGE,"E47.MirrorCS")])]})});
            var sketch = newSketch(context, id + "F33", { "sketchPlane" : qUnion([Q0])});
            skLineSegment(sketch, "E159", {"start": v(-127, 115.18) * mm, "end": v(-330.2, -114.3) * mm, "construction": true});
            skLineSegment(sketch, "E160", {"start": v(-135.47, 115.2) * mm, "end": v(-330.2, -104.72) * mm});
            skLineSegment(sketch, "E161", {"start": v(-135.47, 115.2) * mm, "end": v(-127, 115.18) * mm});
            skLineSegment(sketch, "E162", {"start": v(-127, 115.18) * mm, "end": v(-127, 105.6) * mm});
            skLineSegment(sketch, "E163", {"start": v(-127, 105.6) * mm, "end": v(-321.72, -114.3) * mm});
            skLineSegment(sketch, "E164", {"start": v(-321.72, -114.3) * mm, "end": v(-330.2, -114.3) * mm});
            skLineSegment(sketch, "E165", {"start": v(-330.2, -104.72) * mm, "end": v(-330.2, -114.3) * mm});
            skLineSegment(sketch, "E166", {"start": v(-546.1, 115.71) * mm, "end": v(-342.9, -114.3) * mm, "construction": true});
            skLineSegment(sketch, "E167", {"start": v(-342.9, -114.3) * mm, "end": v(-342.9, -104.7) * mm});
            skLineSegment(sketch, "E168", {"start": v(-342.9, -104.7) * mm, "end": v(-537.4, 115.45) * mm});
            skLineSegment(sketch, "E169", {"start": v(-537.4, 115.45) * mm, "end": v(-546.1, 115.71) * mm});
            skLineSegment(sketch, "E170", {"start": v(-546.1, 106.12) * mm, "end": v(-351.37, -114.3) * mm});
            skLineSegment(sketch, "E171", {"start": v(-351.37, -114.3) * mm, "end": v(-342.9, -114.3) * mm});
            skSolve(sketch);
        }
        {
            var Q0;
            Q0=makeQuery(id+"F10.boolean.opBoolean","COPY",FACE,{"derivedFrom":makeQuery(id+"F10.opExtrude","SWEPT_FACE",FACE,{"disambiguationData":[OSD([sQuery(id+"F9.wireOp",EDGE,"E49")])]})});
            var sketch = newSketch(context, id + "F34", { "sketchPlane" : qUnion([Q0])});
            skLineSegment(sketch, "E172", {"start": v(-746.4, 114.3) * mm, "end": v(-555.82, -45.95) * mm, "construction": true});
            skLineSegment(sketch, "E173", {"start": v(-555.82, -45.95) * mm, "end": v(-567.04, -44.81) * mm});
            skLineSegment(sketch, "E174", {"start": v(-567.04, -44.81) * mm, "end": v(-746.4, 106) * mm});
            skLineSegment(sketch, "E175", {"start": v(-746.4, 106) * mm, "end": v(-746.4, 114.3) * mm});
            skLineSegment(sketch, "E176", {"start": v(-746.4, 114.3) * mm, "end": v(-736.53, 114.3) * mm});
            skLineSegment(sketch, "E177", {"start": v(-736.53, 114.3) * mm, "end": v(-555.82, -37.65) * mm});
            skLineSegment(sketch, "E178", {"start": v(-555.82, -37.65) * mm, "end": v(-555.82, -45.95) * mm});
            skLineSegment(sketch, "E179", {"start": v(-543.11, -48.1) * mm, "end": v(-314.42, 114.61) * mm, "construction": true});
            skLineSegment(sketch, "E180", {"start": v(-314.42, 114.61) * mm, "end": v(-325.4, 114.6) * mm});
            skLineSegment(sketch, "E181", {"start": v(-325.4, 114.6) * mm, "end": v(-543.11, -40.3) * mm});
            skLineSegment(sketch, "E182", {"start": v(-543.11, -40.3) * mm, "end": v(-543.11, -48.1) * mm});
            skLineSegment(sketch, "E183", {"start": v(-543.11, -48.1) * mm, "end": v(-533.43, -49) * mm});
            skLineSegment(sketch, "E184", {"start": v(-533.43, -49) * mm, "end": v(-314.42, 106.82) * mm});
            skLineSegment(sketch, "E185", {"start": v(-314.42, 106.82) * mm, "end": v(-314.42, 114.61) * mm});
            skLineSegment(sketch, "E186", {"start": v(-325.4, 114.6) * mm, "end": v(-314.42, 114.61) * mm});
            skLineSegment(sketch, "E187", {"start": v(-301.71, 114.63) * mm, "end": v(-98.43, -92.46) * mm, "construction": true});
            skLineSegment(sketch, "E188", {"start": v(117.56, 115.18) * mm, "end": v(-85.72, -93.75) * mm, "construction": true});
            skLineSegment(sketch, "E189", {"start": v(-301.71, 114.63) * mm, "end": v(-292.83, 114.64) * mm});
            skLineSegment(sketch, "E190", {"start": v(-292.83, 114.64) * mm, "end": v(-98.43, -83.4) * mm});
            skLineSegment(sketch, "E191", {"start": v(-98.43, -83.4) * mm, "end": v(-98.43, -92.46) * mm});
            skLineSegment(sketch, "E192", {"start": v(-108.3, -91.45) * mm, "end": v(-98.43, -92.46) * mm});
            skLineSegment(sketch, "E193", {"start": v(-108.3, -91.45) * mm, "end": v(-301.71, 105.56) * mm});
            skLineSegment(sketch, "E194", {"start": v(-301.71, 105.56) * mm, "end": v(-301.71, 114.63) * mm});
            skLineSegment(sketch, "E195", {"start": v(-85.72, -93.75) * mm, "end": v(-85.72, -84.64) * mm});
            skLineSegment(sketch, "E196", {"start": v(-85.72, -84.64) * mm, "end": v(108.7, 115.17) * mm});
            skLineSegment(sketch, "E197", {"start": v(108.7, 115.17) * mm, "end": v(117.56, 115.18) * mm});
            skLineSegment(sketch, "E198", {"start": v(117.56, 115.18) * mm, "end": v(117.58, 106.09) * mm});
            skLineSegment(sketch, "E199", {"start": v(117.58, 106.09) * mm, "end": v(-77.66, -94.56) * mm});
            skLineSegment(sketch, "E200", {"start": v(-77.66, -94.56) * mm, "end": v(-85.72, -93.75) * mm});
            skSolve(sketch);
        }
        {
            var Q0;
            Q0 = qSketchRegion(id + "F34", true);
            extrude(context, id + "F35", {"entities" : qUnion([Q0]), "oppositeDirection" : true, "depth" : 12.7 * mm});
        }
        {
            var Q0;
            Q0 = qSketchRegion(id + "F32", true);
            extrude(context, id + "F36", {"entities" : qUnion([Q0]), "oppositeDirection" : true, "depth" : 12.7 * mm});
        }
        {
            var Q0;
            Q0=makeQuery(id+"F10.boolean.opBoolean","COPY",FACE,{"derivedFrom":makeQuery(id+"F10.opExtrude","SWEPT_FACE",FACE,{"disambiguationData":[OSD([sQuery(id+"F9.wireOp",EDGE,"E46"),sQuery(id+"F9.wireOp",EDGE,"E48")])]})});
            var sketch = newSketch(context, id + "F37", { "sketchPlane" : qUnion([Q0])});
            skLineSegment(sketch, "E201.0", {"start": v(135.47, 115.2) * mm, "end": v(330.2, -104.72) * mm});
            skLineSegment(sketch, "E202.0", {"start": v(127, 105.6) * mm, "end": v(321.72, -114.3) * mm});
            skLineSegment(sketch, "E203.0", {"start": v(342.9, -104.7) * mm, "end": v(537.4, 115.45) * mm});
            skLineSegment(sketch, "E204.0", {"start": v(546.1, 106.12) * mm, "end": v(351.37, -114.3) * mm});
            skLineSegment(sketch, "E205.0", {"start": v(537.4, 115.45) * mm, "end": v(546.1, 115.71) * mm});
            skLineSegment(sketch, "E206", {"start": v(546.1, 115.71) * mm, "end": v(546.1, 106.12) * mm});
            skLineSegment(sketch, "E207", {"start": v(351.37, -114.3) * mm, "end": v(342.9, -114.3) * mm});
            skLineSegment(sketch, "E208", {"start": v(342.9, -114.3) * mm, "end": v(342.9, -104.7) * mm});
            skLineSegment(sketch, "E209", {"start": v(330.2, -104.72) * mm, "end": v(330.2, -114.3) * mm});
            skLineSegment(sketch, "E210", {"start": v(330.2, -114.3) * mm, "end": v(321.72, -114.3) * mm});
            skLineSegment(sketch, "E211", {"start": v(127, 105.6) * mm, "end": v(127, 115.18) * mm});
            skLineSegment(sketch, "E212", {"start": v(127, 115.18) * mm, "end": v(135.47, 115.2) * mm});
            skSolve(sketch);
        }
        {
            var Q0;
            Q0 = qSketchRegion(id + "F37", true);
            extrude(context, id + "F38", {"entities" : qUnion([Q0]), "operationType" : NewBodyOperationType.ADD, "oppositeDirection" : true, "depth" : 12.7 * mm});
        }
        {
            var Q0;
            Q0 = qSketchRegion(id + "F33", true);
            var Q1;
            {var subQ7=sQuery(id+"F33.wireOp",EDGE,"E167");Q1=makeQuery(id+"F33.imprint","IMPRINT",FACE,{"disambiguationData":[TD([[makeQuery(id+"F33.imprint","IMPRINT",EDGE,{"derivedFrom":subQ7}),1.0]])]});}
            extrude(context, id + "F39", {"entities" : qUnion([Q0, Q1]), "oppositeDirection" : true, "depth" : 12.7 * mm});
        }
        {
            var Q0;
            Q0=makeQuery(id+"F8.boolean.opBoolean","COPY",FACE,{"derivedFrom":makeQuery(id+"F8.opExtrude","SWEPT_FACE",FACE,{"disambiguationData":[OSD([sQuery(id+"F7.wireOp",EDGE,"E20")])]})});
            var sketch = newSketch(context, id + "F40", { "sketchPlane" : qUnion([Q0])});
            skLineSegment(sketch, "E213", {"start": v(741.5, 76.56) * mm, "end": v(550.02, -82.08) * mm, "construction": true});
            skLineSegment(sketch, "E214", {"start": v(307.48, 89.08) * mm, "end": v(537.26, -82.45) * mm, "construction": true});
            skLineSegment(sketch, "E215", {"start": v(294.72, 89.45) * mm, "end": v(90.47, -95.34) * mm, "construction": true});
            skLineSegment(sketch, "E216", {"start": v(77.7, -95.71) * mm, "end": v(-126.53, 101.6) * mm, "construction": true});
            skLineSegment(sketch, "E217", {"start": v(741.5, 76.56) * mm, "end": v(741.5, 68.32) * mm});
            skLineSegment(sketch, "E218", {"start": v(741.5, 68.32) * mm, "end": v(560.33, -81.79) * mm});
            skLineSegment(sketch, "E219", {"start": v(550.02, -73.84) * mm, "end": v(731.55, 76.56) * mm});
            skLineSegment(sketch, "E220", {"start": v(731.55, 76.56) * mm, "end": v(741.5, 76.56) * mm});
            skLineSegment(sketch, "E221", {"start": v(537.26, -82.45) * mm, "end": v(537.26, -74.53) * mm});
            skLineSegment(sketch, "E222", {"start": v(537.26, -74.53) * mm, "end": v(318.52, 88.76) * mm});
            skLineSegment(sketch, "E223", {"start": v(307.48, 81.15) * mm, "end": v(527.04, -82.75) * mm});
            skLineSegment(sketch, "E224", {"start": v(527.04, -82.75) * mm, "end": v(537.26, -82.45) * mm});
            skLineSegment(sketch, "E225", {"start": v(294.72, 89.45) * mm, "end": v(294.72, 80.88) * mm});
            skLineSegment(sketch, "E226", {"start": v(294.72, 80.88) * mm, "end": v(100.25, -95.05) * mm});
            skLineSegment(sketch, "E227", {"start": v(100.25, -95.05) * mm, "end": v(90.47, -95.34) * mm});
            skLineSegment(sketch, "E228", {"start": v(90.47, -95.34) * mm, "end": v(90.47, -86.77) * mm});
            skLineSegment(sketch, "E229", {"start": v(90.47, -86.77) * mm, "end": v(285.54, 89.71) * mm});
            skLineSegment(sketch, "E230", {"start": v(285.54, 89.71) * mm, "end": v(294.72, 89.45) * mm});
            skLineSegment(sketch, "E231", {"start": v(77.7, -95.71) * mm, "end": v(77.7, -86.88) * mm});
            skLineSegment(sketch, "E232", {"start": v(77.7, -86.88) * mm, "end": v(-117.11, 101.32) * mm});
            skLineSegment(sketch, "E233", {"start": v(-117.11, 101.32) * mm, "end": v(-126.53, 101.6) * mm});
            skLineSegment(sketch, "E234", {"start": v(-126.53, 92.77) * mm, "end": v(68.83, -95.97) * mm});
            skLineSegment(sketch, "E235", {"start": v(68.83, -95.97) * mm, "end": v(77.7, -95.71) * mm});
            skLineSegment(sketch, "E236", {"start": v(550.02, -82.08) * mm, "end": v(560.33, -81.79) * mm});
            skLineSegment(sketch, "E237", {"start": v(307.48, 89.08) * mm, "end": v(318.52, 88.76) * mm});
            skLineSegment(sketch, "E238", {"start": v(-126.53, 92.77) * mm, "end": v(-126.53, 101.6) * mm});
            skSolve(sketch);
        }
        {
            var Q0;
            {var subQ5=sQuery(id+"F5.wireOp",EDGE,"E6.right");var subQ10=sQuery(id+"F0.wireOp",EDGE,"E0.bottom");var subQ18=sQuery(id+"F0.wireOp",EDGE,"E0.top");var subQ21=sQuery(id+"F5.wireOp",EDGE,"E5.right");var subQ40=makeQuery(id+"F2.opExtrude","CAP_FACE",FACE,{"disambiguationData":[OSD([subQ10,subQ18,sQuery(id+"F0.wireOp",EDGE,"E0.left"),sQuery(id+"F0.wireOp",EDGE,"E0.right")])],"isStart":true});Q0=makeQuery(id+"F8.boolean.opBoolean","MERGE",FACE,{"derivedFrom":[makeQuery(id+"F6.boolean.opBoolean","SPLIT",FACE,{"disambiguationData":[TD([makeQuery(id+"F6.opExtrude","SWEPT_FACE",FACE,{"disambiguationData":[OSD([subQ21])]})])],"derivedFrom":subQ40}),makeQuery(id+"F6.boolean.opBoolean","SPLIT",FACE,{"disambiguationData":[TD([makeQuery(id+"F6.opExtrude","SWEPT_FACE",FACE,{"disambiguationData":[OSD([subQ5])]})])],"derivedFrom":subQ40}),makeQuery(id+"F8.opExtrude","SWEPT_FACE",FACE,{"disambiguationData":[OSD([sQuery(id+"F7.wireOp",EDGE,"E26")])]})]});}
            var sketch = newSketch(context, id + "F41", { "sketchPlane" : qUnion([Q0])});
            skLineSegment(sketch, "E239", {"start": v(-127, 101.96) * mm, "end": v(-330.2, -101.6) * mm, "construction": true});
            skLineSegment(sketch, "E240", {"start": v(-546.1, 101.96) * mm, "end": v(-342.9, -101.6) * mm, "construction": true});
            skLineSegment(sketch, "E241", {"start": v(-546.1, 101.96) * mm, "end": v(-546.1, 92.97) * mm});
            skLineSegment(sketch, "E242", {"start": v(-546.1, 92.97) * mm, "end": v(-351.87, -101.6) * mm});
            skLineSegment(sketch, "E243", {"start": v(-351.87, -101.6) * mm, "end": v(-342.9, -101.6) * mm});
            skLineSegment(sketch, "E244", {"start": v(-342.9, -92.61) * mm, "end": v(-537.13, 101.96) * mm});
            skLineSegment(sketch, "E245", {"start": v(-537.13, 101.96) * mm, "end": v(-546.1, 101.96) * mm});
            skLineSegment(sketch, "E246", {"start": v(-330.2, -101.6) * mm, "end": v(-321.23, -101.6) * mm});
            skLineSegment(sketch, "E247", {"start": v(-321.23, -101.6) * mm, "end": v(-127, 92.97) * mm});
            skLineSegment(sketch, "E248", {"start": v(-127, 92.97) * mm, "end": v(-127, 101.96) * mm});
            skLineSegment(sketch, "E249", {"start": v(-135.97, 101.96) * mm, "end": v(-330.2, -92.61) * mm});
            skLineSegment(sketch, "E250", {"start": v(-330.2, -92.61) * mm, "end": v(-330.2, -101.6) * mm});
            skSolve(sketch);
        }
        {
            var Q0;
            Q0=makeQuery(id+"F40.imprint","IMPRINT",FACE,{"disambiguationData":[TD([[makeQuery(id+"F40.imprint","IMPRINT",EDGE,{"derivedFrom":sQuery(id+"F40.wireOp",EDGE,"E225")}),1.0]])]});
            var Q1;
            Q1=makeQuery(id+"F40.imprint","IMPRINT",FACE,{"disambiguationData":[TD([[makeQuery(id+"F40.imprint","IMPRINT",EDGE,{"derivedFrom":sQuery(id+"F40.wireOp",EDGE,"E221")}),1.0]])]});
            var Q2;
            Q2=makeQuery(id+"F40.imprint","IMPRINT",FACE,{"disambiguationData":[TD([[makeQuery(id+"F40.imprint","IMPRINT",EDGE,{"derivedFrom":sQuery(id+"F40.wireOp",EDGE,"E217")}),1.0]])]});
            var Q3;
            Q3=makeQuery(id+"F40.imprint","IMPRINT",FACE,{"disambiguationData":[TD([[makeQuery(id+"F40.imprint","IMPRINT",EDGE,{"derivedFrom":sQuery(id+"F40.wireOp",EDGE,"E231")}),1.0]])]});
            extrude(context, id + "F42", {"entities" : qUnion([Q0, Q1, Q2, Q3]), "oppositeDirection" : true, "depth" : 12.7 * mm});
        }
        {
            var Q0;
            Q0=makeQuery(id+"F41.imprint","IMPRINT",FACE,{"disambiguationData":[TD([[makeQuery(id+"F41.imprint","IMPRINT",EDGE,{"derivedFrom":sQuery(id+"F41.wireOp",EDGE,"E246")}),1.0]])]});
            var Q1;
            Q1=makeQuery(id+"F41.imprint","IMPRINT",FACE,{"disambiguationData":[TD([[makeQuery(id+"F41.imprint","IMPRINT",EDGE,{"derivedFrom":sQuery(id+"F41.wireOp",EDGE,"E241")}),-1.0]])]});
            extrude(context, id + "F43", {"entities" : qUnion([Q0, Q1]), "oppositeDirection" : true, "depth" : 12.7 * mm});
        }
        {
            var Q0;
            {var subQ1=makeQuery(id+"F10.boolean.opBoolean","COPY",FACE,{"derivedFrom":makeQuery(id+"F10.opExtrude","SWEPT_FACE",FACE,{"disambiguationData":[OSD([sQuery(id+"F9.wireOp",EDGE,"E51")])]})});var subQ5=sQuery(id+"F5.wireOp",EDGE,"E12.left");var subQ6=makeQuery(id+"F6.opExtrude","SWEPT_FACE",FACE,{"disambiguationData":[OSD([subQ5])]});var subQ7=sQuery(id+"F5.wireOp",EDGE,"E8.right");var subQ12=sQuery(id+"F5.wireOp",EDGE,"E7.right");var subQ17=sQuery(id+"F5.wireOp",EDGE,"E6.right");var subQ22=sQuery(id+"F0.wireOp",EDGE,"E0.bottom");var subQ30=sQuery(id+"F0.wireOp",EDGE,"E0.top");var subQ33=sQuery(id+"F5.wireOp",EDGE,"E5.right");var subQ45=sQuery(id+"F0.wireOp",EDGE,"E0.left");var subQ46=makeQuery(id+"F2.opExtrude","CAP_FACE",FACE,{"disambiguationData":[OSD([subQ22,subQ30,subQ45,sQuery(id+"F0.wireOp",EDGE,"E0.right")])],"isStart":false});var subQ47=makeQuery(id+"F6.boolean.opBoolean","SPLIT",FACE,{"disambiguationData":[TD([subQ6])],"derivedFrom":subQ46});var subQ48=makeQuery(id+"F10.boolean.opBoolean","COPY",FACE,{"derivedFrom":makeQuery(id+"F10.opExtrude","SWEPT_FACE",FACE,{"disambiguationData":[OSD([sQuery(id+"F9.wireOp",EDGE,"E49")])]})});var subQ50=makeQuery(id+"F6.opExtrude","SWEPT_FACE",FACE,{"disambiguationData":[OSD([subQ7])]});var subQ53=makeQuery(id+"F6.boolean.opBoolean","SPLIT",FACE,{"disambiguationData":[TD([subQ50])],"derivedFrom":subQ46});var subQ57=makeQuery(id+"F6.opExtrude","SWEPT_FACE",FACE,{"disambiguationData":[OSD([subQ12])]});var subQ59=makeQuery(id+"F6.boolean.opBoolean","SPLIT",FACE,{"disambiguationData":[TD([subQ57])],"derivedFrom":subQ46});var subQ62=makeQuery(id+"F6.opExtrude","SWEPT_FACE",FACE,{"disambiguationData":[OSD([subQ17])]});var subQ65=makeQuery(id+"F6.boolean.opBoolean","SPLIT",FACE,{"disambiguationData":[TD([subQ62])],"derivedFrom":subQ46});var subQ67=makeQuery(id+"F6.opExtrude","SWEPT_FACE",FACE,{"disambiguationData":[OSD([subQ33])]});var subQ70=makeQuery(id+"F6.boolean.opBoolean","SPLIT",FACE,{"disambiguationData":[TD([subQ67])],"derivedFrom":subQ46});Q0=makeQuery(id+"F14.boolean.opBoolean","MERGE",FACE,{"derivedFrom":[makeQuery(id+"F6.boolean.opBoolean","SPLIT",FACE,{"disambiguationData":[TD([makeQuery(id+"F2.opExtrude","SWEPT_FACE",FACE,{"disambiguationData":[OSD([subQ45])]})])],"derivedFrom":subQ46}),makeQuery(id+"F12.boolean.opBoolean","SPLIT",FACE,{"disambiguationData":[TD([makeQuery(id+"F12.opExtrude","SWEPT_FACE",FACE,{"disambiguationData":[OSD([sQuery(id+"F11.wireOp",EDGE,"E62")])]})])],"derivedFrom":subQ70}),makeQuery(id+"F12.boolean.opBoolean","SPLIT",FACE,{"disambiguationData":[TD([makeQuery(id+"F12.opExtrude","SWEPT_FACE",FACE,{"disambiguationData":[OSD([sQuery(id+"F11.wireOp",EDGE,"E61")])]})])],"derivedFrom":subQ70}),makeQuery(id+"F12.boolean.opBoolean","SPLIT",FACE,{"disambiguationData":[TD([makeQuery(id+"F12.opExtrude","SWEPT_FACE",FACE,{"disambiguationData":[OSD([sQuery(id+"F11.wireOp",EDGE,"E56.0")])]})])],"derivedFrom":subQ65}),makeQuery(id+"F12.boolean.opBoolean","SPLIT",FACE,{"disambiguationData":[TD([makeQuery(id+"F12.opExtrude","SWEPT_FACE",FACE,{"disambiguationData":[OSD([sQuery(id+"F11.wireOp",EDGE,"E57.0")])]})])],"derivedFrom":subQ65}),makeQuery(id+"F12.boolean.opBoolean","SPLIT",FACE,{"disambiguationData":[TD([subQ48])],"derivedFrom":subQ59}),makeQuery(id+"F12.boolean.opBoolean","SPLIT",FACE,{"disambiguationData":[TD([subQ1])],"derivedFrom":subQ59}),makeQuery(id+"F12.boolean.opBoolean","SPLIT",FACE,{"disambiguationData":[TD([subQ48])],"derivedFrom":subQ53}),makeQuery(id+"F12.boolean.opBoolean","SPLIT",FACE,{"disambiguationData":[TD([subQ1])],"derivedFrom":subQ53}),makeQuery(id+"F12.boolean.opBoolean","SPLIT",FACE,{"disambiguationData":[TD([subQ48])],"derivedFrom":subQ47}),makeQuery(id+"F12.boolean.opBoolean","SPLIT",FACE,{"disambiguationData":[TD([subQ1])],"derivedFrom":subQ47}),makeQuery(id+"F14.opExtrude","SWEPT_FACE",FACE,{"disambiguationData":[OSD([sQuery(id+"F13.wireOp",EDGE,"E100.top")])]})]});}
            var sketch = newSketch(context, id + "F44", { "sketchPlane" : qUnion([Q0])});
            skLineSegment(sketch, "E251", {"start": v(762, 88.9) * mm, "end": v(762, -88.9) * mm});
            skLineSegment(sketch, "E252", {"start": v(762, 88.9) * mm, "end": v(-114.3, 114.3) * mm});
            skLineSegment(sketch, "E253", {"start": v(-114.3, -114.3) * mm, "end": v(762, -88.9) * mm});
            skLineSegment(sketch, "E254", {"start": v(-114.3, -114.3) * mm, "end": v(-114.3, 114.3) * mm});
            skSolve(sketch);
        }
        {
            var Q0;
            Q0 = qSketchRegion(id + "F44", true);
            extrude(context, id + "F45", {"entities" : qUnion([Q0]), "depth" : 2.54 * mm});
        }
        {
            var Q0;
            Q0=makeQuery(id+"F2.opExtrude","SWEPT_FACE",FACE,{"disambiguationData":[OSD([sQuery(id+"F0.wireOp",EDGE,"E0.left")])]});
            var sketch = newSketch(context, id + "F46", { "sketchPlane" : qUnion([Q0])});
            skLineSegment(sketch, "E255.bottom", {"start": v(-88.9, 127) * mm, "end": v(88.9, 127) * mm});
            skLineSegment(sketch, "E255.top", {"start": v(-88.9, -38.1) * mm, "end": v(88.9, -38.1) * mm});
            skLineSegment(sketch, "E255.left", {"start": v(-88.9, 127) * mm, "end": v(-88.9, -38.1) * mm});
            skLineSegment(sketch, "E255.right", {"start": v(88.9, 127) * mm, "end": v(88.9, -38.1) * mm});
            skSolve(sketch);
        }
        {
            var Q0;
            Q0 = qSketchRegion(id + "F46", true);
            extrude(context, id + "F47", {"entities" : qUnion([Q0]), "depth" : 2.54 * mm});
        }
        {
            var Q0;
            {var subQ1=makeQuery(id+"F10.boolean.opBoolean","COPY",FACE,{"derivedFrom":makeQuery(id+"F10.opExtrude","SWEPT_FACE",FACE,{"disambiguationData":[OSD([sQuery(id+"F9.wireOp",EDGE,"E51")])]})});var subQ5=sQuery(id+"F5.wireOp",EDGE,"E12.left");var subQ6=makeQuery(id+"F6.opExtrude","SWEPT_FACE",FACE,{"disambiguationData":[OSD([subQ5])]});var subQ7=sQuery(id+"F5.wireOp",EDGE,"E8.right");var subQ12=sQuery(id+"F5.wireOp",EDGE,"E7.right");var subQ17=sQuery(id+"F5.wireOp",EDGE,"E6.right");var subQ22=sQuery(id+"F0.wireOp",EDGE,"E0.bottom");var subQ30=sQuery(id+"F0.wireOp",EDGE,"E0.top");var subQ33=sQuery(id+"F5.wireOp",EDGE,"E5.right");var subQ45=sQuery(id+"F0.wireOp",EDGE,"E0.left");var subQ46=makeQuery(id+"F2.opExtrude","CAP_FACE",FACE,{"disambiguationData":[OSD([subQ22,subQ30,subQ45,sQuery(id+"F0.wireOp",EDGE,"E0.right")])],"isStart":false});var subQ47=makeQuery(id+"F6.boolean.opBoolean","SPLIT",FACE,{"disambiguationData":[TD([subQ6])],"derivedFrom":subQ46});var subQ48=makeQuery(id+"F10.boolean.opBoolean","COPY",FACE,{"derivedFrom":makeQuery(id+"F10.opExtrude","SWEPT_FACE",FACE,{"disambiguationData":[OSD([sQuery(id+"F9.wireOp",EDGE,"E49")])]})});var subQ50=makeQuery(id+"F6.opExtrude","SWEPT_FACE",FACE,{"disambiguationData":[OSD([subQ7])]});var subQ53=makeQuery(id+"F6.boolean.opBoolean","SPLIT",FACE,{"disambiguationData":[TD([subQ50])],"derivedFrom":subQ46});var subQ57=makeQuery(id+"F6.opExtrude","SWEPT_FACE",FACE,{"disambiguationData":[OSD([subQ12])]});var subQ59=makeQuery(id+"F6.boolean.opBoolean","SPLIT",FACE,{"disambiguationData":[TD([subQ57])],"derivedFrom":subQ46});var subQ62=makeQuery(id+"F6.opExtrude","SWEPT_FACE",FACE,{"disambiguationData":[OSD([subQ17])]});var subQ65=makeQuery(id+"F6.boolean.opBoolean","SPLIT",FACE,{"disambiguationData":[TD([subQ62])],"derivedFrom":subQ46});var subQ67=makeQuery(id+"F6.opExtrude","SWEPT_FACE",FACE,{"disambiguationData":[OSD([subQ33])]});var subQ70=makeQuery(id+"F6.boolean.opBoolean","SPLIT",FACE,{"disambiguationData":[TD([subQ67])],"derivedFrom":subQ46});Q0=makeQuery(id+"F14.boolean.opBoolean","MERGE",FACE,{"derivedFrom":[makeQuery(id+"F6.boolean.opBoolean","SPLIT",FACE,{"disambiguationData":[TD([makeQuery(id+"F2.opExtrude","SWEPT_FACE",FACE,{"disambiguationData":[OSD([subQ45])]})])],"derivedFrom":subQ46}),makeQuery(id+"F12.boolean.opBoolean","SPLIT",FACE,{"disambiguationData":[TD([makeQuery(id+"F12.opExtrude","SWEPT_FACE",FACE,{"disambiguationData":[OSD([sQuery(id+"F11.wireOp",EDGE,"E62")])]})])],"derivedFrom":subQ70}),makeQuery(id+"F12.boolean.opBoolean","SPLIT",FACE,{"disambiguationData":[TD([makeQuery(id+"F12.opExtrude","SWEPT_FACE",FACE,{"disambiguationData":[OSD([sQuery(id+"F11.wireOp",EDGE,"E61")])]})])],"derivedFrom":subQ70}),makeQuery(id+"F12.boolean.opBoolean","SPLIT",FACE,{"disambiguationData":[TD([makeQuery(id+"F12.opExtrude","SWEPT_FACE",FACE,{"disambiguationData":[OSD([sQuery(id+"F11.wireOp",EDGE,"E56.0")])]})])],"derivedFrom":subQ65}),makeQuery(id+"F12.boolean.opBoolean","SPLIT",FACE,{"disambiguationData":[TD([makeQuery(id+"F12.opExtrude","SWEPT_FACE",FACE,{"disambiguationData":[OSD([sQuery(id+"F11.wireOp",EDGE,"E57.0")])]})])],"derivedFrom":subQ65}),makeQuery(id+"F12.boolean.opBoolean","SPLIT",FACE,{"disambiguationData":[TD([subQ48])],"derivedFrom":subQ59}),makeQuery(id+"F12.boolean.opBoolean","SPLIT",FACE,{"disambiguationData":[TD([subQ1])],"derivedFrom":subQ59}),makeQuery(id+"F12.boolean.opBoolean","SPLIT",FACE,{"disambiguationData":[TD([subQ48])],"derivedFrom":subQ53}),makeQuery(id+"F12.boolean.opBoolean","SPLIT",FACE,{"disambiguationData":[TD([subQ1])],"derivedFrom":subQ53}),makeQuery(id+"F12.boolean.opBoolean","SPLIT",FACE,{"disambiguationData":[TD([subQ48])],"derivedFrom":subQ47}),makeQuery(id+"F12.boolean.opBoolean","SPLIT",FACE,{"disambiguationData":[TD([subQ1])],"derivedFrom":subQ47}),makeQuery(id+"F14.opExtrude","SWEPT_FACE",FACE,{"disambiguationData":[OSD([sQuery(id+"F13.wireOp",EDGE,"E100.top")])]})]});}
            var sketch = newSketch(context, id + "F48", { "sketchPlane" : qUnion([Q0])});
            skLineSegment(sketch, "E256.bottom", {"start": v(-558.8, 114.3) * mm, "end": v(-127, 114.3) * mm});
            skLineSegment(sketch, "E256.top", {"start": v(-558.8, -114.3) * mm, "end": v(-127, -114.3) * mm});
            skLineSegment(sketch, "E256.left", {"start": v(-558.8, 114.3) * mm, "end": v(-558.8, -114.3) * mm});
            skLineSegment(sketch, "E257", {"start": v(-127, 114.3) * mm, "end": v(-114.3, 114.3) * mm});
            skLineSegment(sketch, "E258", {"start": v(-114.3, 114.3) * mm, "end": v(-114.3, -114.3) * mm});
            skLineSegment(sketch, "E259", {"start": v(-114.3, -114.3) * mm, "end": v(-127, -114.3) * mm});
            skSolve(sketch);
        }
        {
            var Q0;
            Q0 = qSketchRegion(id + "F48", true);
            extrude(context, id + "F49", {"entities" : qUnion([Q0]), "depth" : 2.54 * mm});
        }
        {
            var Q0;
            Q0=makeQuery(id+"F8.boolean.opBoolean","COPY",FACE,{"derivedFrom":makeQuery(id+"F8.opExtrude","SWEPT_FACE",FACE,{"disambiguationData":[OSD([sQuery(id+"F7.wireOp",EDGE,"E14")])]})});
            var sketch = newSketch(context, id + "F50", { "sketchPlane" : qUnion([Q0])});
            skLineSegment(sketch, "E260", {"start": v(-707.9, 77.57) * mm, "end": v(-494.86, 114.3) * mm});
            skLineSegment(sketch, "E261", {"start": v(-494.86, 114.3) * mm, "end": v(-494.86, -114.3) * mm});
            skLineSegment(sketch, "E262", {"start": v(-494.86, -114.3) * mm, "end": v(-707.9, -77.57) * mm});
            skLineSegment(sketch, "E263", {"start": v(-707.9, -77.57) * mm, "end": v(-707.9, 77.57) * mm});
            skSolve(sketch);
        }
        {
            var Q0;
            Q0 = qSketchRegion(id + "F50", true);
            extrude(context, id + "F51", {"entities" : qUnion([Q0]), "depth" : 2.54 * mm});
        }
        {
            var Q0;
            Q0=makeQuery(id+"F2.opExtrude","SWEPT_FACE",FACE,{"disambiguationData":[OSD([sQuery(id+"F0.wireOp",EDGE,"E0.right")])]});
            var sketch = newSketch(context, id + "F52", { "sketchPlane" : qUnion([Q0])});
            skLineSegment(sketch, "E264.bottom", {"start": v(-77.57, 63.02) * mm, "end": v(77.57, 63.02) * mm});
            skLineSegment(sketch, "E264.top", {"start": v(-77.57, -38.1) * mm, "end": v(77.57, -38.1) * mm});
            skLineSegment(sketch, "E264.left", {"start": v(-77.57, 63.02) * mm, "end": v(-77.57, -38.1) * mm});
            skLineSegment(sketch, "E264.right", {"start": v(77.57, 63.02) * mm, "end": v(77.57, -38.1) * mm});
            skSolve(sketch);
        }
        {
            var Q0;
            Q0 = qSketchRegion(id + "F52", true);
            extrude(context, id + "F53", {"entities" : qUnion([Q0]), "depth" : 2.54 * mm});
        }
        {
            var Q0;
            Q0=makeQuery(id+"F10.boolean.opBoolean","COPY",FACE,{"derivedFrom":makeQuery(id+"F10.opExtrude","SWEPT_FACE",FACE,{"disambiguationData":[OSD([sQuery(id+"F9.wireOp",EDGE,"E53")])]})});
            var sketch = newSketch(context, id + "F54", { "sketchPlane" : qUnion([Q0])});
            skLineSegment(sketch, "E265", {"start": v(-529.56, -127) * mm, "end": v(-736.05, -38.1) * mm});
            skLineSegment(sketch, "E266", {"start": v(-736.05, -38.1) * mm, "end": v(-736.05, 63.02) * mm});
            skLineSegment(sketch, "E267", {"start": v(-736.05, 63.02) * mm, "end": v(-529.56, 127) * mm});
            skLineSegment(sketch, "E268", {"start": v(-529.56, 127) * mm, "end": v(-529.56, -127) * mm});
            skSolve(sketch);
        }
        {
            var Q0;
            Q0 = qSketchRegion(id + "F54", true);
            extrude(context, id + "F55", {"entities" : qUnion([Q0]), "depth" : 2.54 * mm});
        }
        {
            var Q0;
            {var subQ0=sQuery(id+"F9.wireOp",EDGE,"E50");var subQ1=sQuery(id+"F9.wireOp",EDGE,"E47.MirrorCS");Q0=makeQuery(id+"F39.boolean.opBoolean","MERGE",FACE,{"derivedFrom":[makeQuery(id+"F10.boolean.opBoolean","COPY",FACE,{"derivedFrom":makeQuery(id+"F10.opExtrude","SWEPT_FACE",FACE,{"disambiguationData":[OSD([subQ1,subQ0])]})}),makeQuery(id+"F39.opExtrude","CAP_FACE",FACE,{"disambiguationData":[OSD([sQuery(id+"F33.wireOp",EDGE,"E160"),sQuery(id+"F33.wireOp",EDGE,"E161"),sQuery(id+"F33.wireOp",EDGE,"E162"),sQuery(id+"F33.wireOp",EDGE,"E163"),sQuery(id+"F33.wireOp",EDGE,"E164"),sQuery(id+"F33.wireOp",EDGE,"E165")])],"isStart":true}),makeQuery(id+"F39.opExtrude","CAP_FACE",FACE,{"disambiguationData":[OSD([subQ1,subQ0,sQuery(id+"F13.wireOp",EDGE,"E80.3"),sQuery(id+"F13.wireOp",EDGE,"E86.0.1"),sQuery(id+"F33.wireOp",EDGE,"E167"),sQuery(id+"F33.wireOp",EDGE,"E168"),sQuery(id+"F33.wireOp",EDGE,"E169"),sQuery(id+"F33.wireOp",EDGE,"E170")])],"isStart":true})]});}
            var sketch = newSketch(context, id + "F56", { "sketchPlane" : qUnion([Q0])});
            skLineSegment(sketch, "E269.bottom", {"start": v(-114.3, -127) * mm, "end": v(-558.8, -127) * mm});
            skLineSegment(sketch, "E269.top", {"start": v(-114.3, 127) * mm, "end": v(-558.8, 127) * mm});
            skLineSegment(sketch, "E269.left", {"start": v(-114.3, -127) * mm, "end": v(-114.3, 127) * mm});
            skLineSegment(sketch, "E269.right", {"start": v(-558.8, -127) * mm, "end": v(-558.8, 127) * mm});
            skSolve(sketch);
        }
        {
            var Q0;
            Q0 = qSketchRegion(id + "F56", true);
            extrude(context, id + "F57", {"entities" : qUnion([Q0]), "depth" : 2.54 * mm});
        }
        {
            var Q0;
            Q0=makeQuery(id+"F10.boolean.opBoolean","COPY",FACE,{"derivedFrom":makeQuery(id+"F10.opExtrude","SWEPT_FACE",FACE,{"disambiguationData":[OSD([sQuery(id+"F9.wireOp",EDGE,"E51")])]})});
            var sketch = newSketch(context, id + "F58", { "sketchPlane" : qUnion([Q0])});
            skLineSegment(sketch, "E270", {"start": v(759.1, 127) * mm, "end": v(-117.56, 127) * mm});
            skLineSegment(sketch, "E271", {"start": v(-117.56, 127) * mm, "end": v(-117.56, -127) * mm});
            skLineSegment(sketch, "E272", {"start": v(-117.56, -127) * mm, "end": v(759.1, -38.1) * mm});
            skLineSegment(sketch, "E273", {"start": v(759.1, -38.1) * mm, "end": v(759.1, 127) * mm});
            skSolve(sketch);
        }
        {
            var Q0;
            Q0 = qSketchRegion(id + "F58", true);
            extrude(context, id + "F59", {"entities" : qUnion([Q0]), "depth" : 2.54 * mm});
        }
        {
            var Q0;
            Q0=makeQuery(id+"F10.boolean.opBoolean","COPY",FACE,{"derivedFrom":makeQuery(id+"F10.opExtrude","SWEPT_FACE",FACE,{"disambiguationData":[OSD([sQuery(id+"F9.wireOp",EDGE,"E49")])]})});
            var sketch = newSketch(context, id + "F60", { "sketchPlane" : qUnion([Q0])});
            skLineSegment(sketch, "E274", {"start": v(-759.1, 127) * mm, "end": v(117.56, 127) * mm});
            skLineSegment(sketch, "E275", {"start": v(117.56, 127) * mm, "end": v(117.56, -127) * mm});
            skLineSegment(sketch, "E276", {"start": v(117.56, -127) * mm, "end": v(-759.1, -38.1) * mm});
            skLineSegment(sketch, "E277", {"start": v(-759.1, -38.1) * mm, "end": v(-759.1, 127) * mm});
            skSolve(sketch);
        }
        {
            var Q0;
            Q0 = qSketchRegion(id + "F60", true);
            extrude(context, id + "F61", {"entities" : qUnion([Q0]), "depth" : 2.54 * mm});
        }
        {
            var Q0;
            Q0=makeQuery(id+"F38.boolean.opBoolean","MERGE",FACE,{"derivedFrom":[makeQuery(id+"F10.boolean.opBoolean","COPY",FACE,{"derivedFrom":makeQuery(id+"F10.opExtrude","SWEPT_FACE",FACE,{"disambiguationData":[OSD([sQuery(id+"F9.wireOp",EDGE,"E46"),sQuery(id+"F9.wireOp",EDGE,"E48")])]})}),makeQuery(id+"F38.opExtrude","CAP_FACE",FACE,{"disambiguationData":[OSD([sQuery(id+"F37.wireOp",EDGE,"E201.0"),sQuery(id+"F37.wireOp",EDGE,"E202.0"),sQuery(id+"F37.wireOp",EDGE,"E209"),sQuery(id+"F37.wireOp",EDGE,"E210"),sQuery(id+"F37.wireOp",EDGE,"E211"),sQuery(id+"F37.wireOp",EDGE,"E212")])],"isStart":true}),makeQuery(id+"F38.opExtrude","CAP_FACE",FACE,{"disambiguationData":[OSD([sQuery(id+"F37.wireOp",EDGE,"E203.0"),sQuery(id+"F37.wireOp",EDGE,"E204.0"),sQuery(id+"F37.wireOp",EDGE,"E205.0"),sQuery(id+"F37.wireOp",EDGE,"E206"),sQuery(id+"F37.wireOp",EDGE,"E207"),sQuery(id+"F37.wireOp",EDGE,"E208")])],"isStart":true})]});
            var sketch = newSketch(context, id + "F62", { "sketchPlane" : qUnion([Q0])});
            skLineSegment(sketch, "E278.bottom", {"start": v(114.3, 127) * mm, "end": v(558.8, 127) * mm});
            skLineSegment(sketch, "E278.top", {"start": v(114.3, -127) * mm, "end": v(558.8, -127) * mm});
            skLineSegment(sketch, "E278.left", {"start": v(114.3, 127) * mm, "end": v(114.3, -127) * mm});
            skLineSegment(sketch, "E278.right", {"start": v(558.8, 127) * mm, "end": v(558.8, -127) * mm});
            skSolve(sketch);
        }
        {
            var Q0;
            Q0 = qSketchRegion(id + "F62", true);
            extrude(context, id + "F63", {"entities" : qUnion([Q0]), "depth" : 2.54 * mm});
        }
        {
            var Q0;
            Q0=makeQuery(id+"F10.boolean.opBoolean","COPY",FACE,{"derivedFrom":makeQuery(id+"F10.opExtrude","SWEPT_FACE",FACE,{"disambiguationData":[OSD([sQuery(id+"F9.wireOp",EDGE,"E52")])]})});
            var sketch = newSketch(context, id + "F64", { "sketchPlane" : qUnion([Q0])});
            skLineSegment(sketch, "E279", {"start": v(736.05, 63.02) * mm, "end": v(529.56, 127) * mm});
            skLineSegment(sketch, "E280", {"start": v(529.56, 127) * mm, "end": v(529.56, -127) * mm});
            skLineSegment(sketch, "E281", {"start": v(529.56, -127) * mm, "end": v(736.05, -38.1) * mm});
            skLineSegment(sketch, "E282", {"start": v(736.05, -38.1) * mm, "end": v(736.05, 63.02) * mm});
            skSolve(sketch);
        }
        {
            var Q0;
            Q0 = qSketchRegion(id + "F64", true);
            extrude(context, id + "F65", {"entities" : qUnion([Q0]), "depth" : 2.54 * mm});
        }
        {
            var Q0;
            Q0=makeQuery(id+"F8.boolean.opBoolean","COPY",FACE,{"derivedFrom":makeQuery(id+"F8.opExtrude","SWEPT_FACE",FACE,{"disambiguationData":[OSD([sQuery(id+"F7.wireOp",EDGE,"E19")])]})});
            var sketch = newSketch(context, id + "F66", { "sketchPlane" : qUnion([Q0])});
            skLineSegment(sketch, "E283", {"start": v(-682.84, -77.57) * mm, "end": v(-461.04, -114.3) * mm});
            skLineSegment(sketch, "E284", {"start": v(-461.04, -114.3) * mm, "end": v(-461.04, 114.3) * mm});
            skLineSegment(sketch, "E285", {"start": v(-461.04, 114.3) * mm, "end": v(-682.84, 77.57) * mm});
            skLineSegment(sketch, "E286", {"start": v(-682.84, 77.57) * mm, "end": v(-682.84, -77.57) * mm});
            skSolve(sketch);
        }
        {
            var Q0;
            Q0 = qSketchRegion(id + "F66", true);
            extrude(context, id + "F67", {"entities" : qUnion([Q0]), "depth" : 2.54 * mm});
        }
        {
            var Q0;
            {var subQ5=sQuery(id+"F5.wireOp",EDGE,"E6.right");var subQ10=sQuery(id+"F0.wireOp",EDGE,"E0.bottom");var subQ18=sQuery(id+"F0.wireOp",EDGE,"E0.top");var subQ21=sQuery(id+"F5.wireOp",EDGE,"E5.right");var subQ40=makeQuery(id+"F2.opExtrude","CAP_FACE",FACE,{"disambiguationData":[OSD([subQ10,subQ18,sQuery(id+"F0.wireOp",EDGE,"E0.left"),sQuery(id+"F0.wireOp",EDGE,"E0.right")])],"isStart":true});Q0=makeQuery(id+"F8.boolean.opBoolean","MERGE",FACE,{"derivedFrom":[makeQuery(id+"F6.boolean.opBoolean","SPLIT",FACE,{"disambiguationData":[TD([makeQuery(id+"F6.opExtrude","SWEPT_FACE",FACE,{"disambiguationData":[OSD([subQ21])]})])],"derivedFrom":subQ40}),makeQuery(id+"F6.boolean.opBoolean","SPLIT",FACE,{"disambiguationData":[TD([makeQuery(id+"F6.opExtrude","SWEPT_FACE",FACE,{"disambiguationData":[OSD([subQ5])]})])],"derivedFrom":subQ40}),makeQuery(id+"F8.opExtrude","SWEPT_FACE",FACE,{"disambiguationData":[OSD([sQuery(id+"F7.wireOp",EDGE,"E26")])]})]});}
            var sketch = newSketch(context, id + "F68", { "sketchPlane" : qUnion([Q0])});
            skLineSegment(sketch, "E287.bottom", {"start": v(-114.3, -114.3) * mm, "end": v(-558.8, -114.3) * mm});
            skLineSegment(sketch, "E287.top", {"start": v(-114.3, 114.3) * mm, "end": v(-558.8, 114.3) * mm});
            skLineSegment(sketch, "E287.left", {"start": v(-114.3, -114.3) * mm, "end": v(-114.3, 114.3) * mm});
            skLineSegment(sketch, "E287.right", {"start": v(-558.8, -114.3) * mm, "end": v(-558.8, 114.3) * mm});
            skSolve(sketch);
        }
        {
            var Q0;
            Q0 = qSketchRegion(id + "F68", true);
            extrude(context, id + "F69", {"entities" : qUnion([Q0]), "depth" : 2.54 * mm});
        }
        {
            var Q0;
            Q0=makeQuery(id+"F8.boolean.opBoolean","COPY",FACE,{"derivedFrom":makeQuery(id+"F8.opExtrude","SWEPT_FACE",FACE,{"disambiguationData":[OSD([sQuery(id+"F7.wireOp",EDGE,"E20")])]})});
            var sketch = newSketch(context, id + "F70", { "sketchPlane" : qUnion([Q0])});
            skLineSegment(sketch, "E288", {"start": v(754.26, -88.9) * mm, "end": v(-126.53, -114.3) * mm});
            skLineSegment(sketch, "E289", {"start": v(-126.53, -114.3) * mm, "end": v(-126.53, 114.3) * mm});
            skLineSegment(sketch, "E290", {"start": v(-126.53, 114.3) * mm, "end": v(754.26, 88.9) * mm});
            skLineSegment(sketch, "E291", {"start": v(754.26, 88.9) * mm, "end": v(754.26, -88.9) * mm});
            skSolve(sketch);
        }
        {
            var Q0;
            Q0 = qSketchRegion(id + "F70", true);
            extrude(context, id + "F71", {"entities" : qUnion([Q0]), "depth" : 2.54 * mm});
        }
    });
